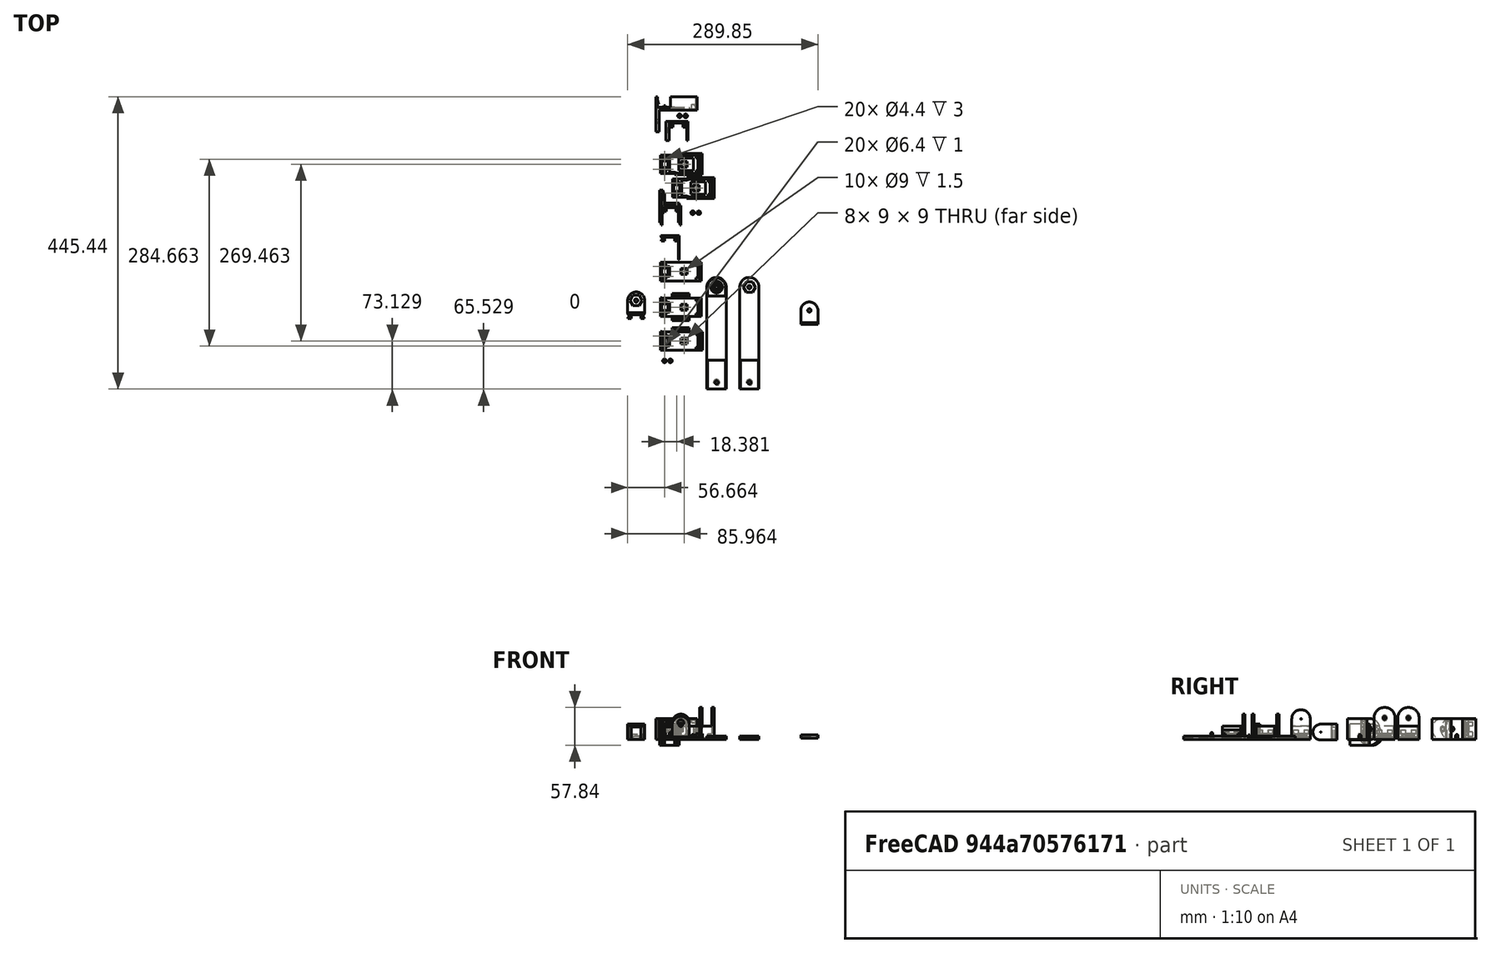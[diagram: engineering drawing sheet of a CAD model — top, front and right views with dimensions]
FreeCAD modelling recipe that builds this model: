
FCSTD DOCUMENT  (FreeCAD 0.18.4R)
Label: camera
License: All rights reserved
LicenseURL: http://en.wikipedia.org/wiki/All_rights_reserved
objects: Part::Extrusion×95, Part::Part2DObjectPython×85, Part::Feature×60, Part::MultiFuse×57, Part::FeaturePython×53, Part::Cut×43, App::DocumentObjectGroup×22, Part::MultiCommon×2, Part::Sphere×2, Part::Cone×1
note: 398 computed .brp shape members not serialized (recipe doc carries the construction recipe); baked Part::Feature solids carry a one-line shape summary decoded from their .brp

FEATURE [Part::MultiFuse] Fusion005002002014004003003002003
  Placement = pos=(31.9244,58.1866,-2) rot=(0,0,1;0rad)
FEATURE [Part::Feature] Fusion005002002014004003003001  label="Fusion005002002014004003004"
  shape: bbox 26 x 40.3 x 22 mm, 31 faces (baked)
FEATURE [Part::Part2DObjectPython] Rectangle  # Draft 2D object (typed FeaturePython)
  ChamferSize = 0
  Columns = 1
  FilletRadius = 0
  Height = 58
  Length = 28.2
  MakeFace = true
  Placement = pos=(-309.476,-65.7008,-5.13395) rot=(0.707107,0.707107,0;3.14159rad)
  Rows = 1
FEATURE [Part::Part2DObjectPython] Circle  # Draft 2D object (typed FeaturePython)
  FirstAngle = 0
  LastAngle = 0
  MakeFace = true
  Placement = pos=(-279.976,-51.6008,-5.13395) rot=(0.707107,0.707107,0;3.14159rad)
  Radius = 4.26
FEATURE [Part::Extrusion] Extrusion
  Base = -> Rectangle
  Dir = (0,0,2)
  DirMode = 0
  FaceMakerClass = Part::FaceMakerBullseye
  LengthFwd = 0
  LengthRev = 0
  Solid = true
  Symmetric = false
FEATURE [Part::Extrusion] Extrusion001
  Base = -> Circle
  Dir = (9.2e-15,2e-15,34.9207)
  DirMode = 0
  FaceMakerClass = Part::FaceMakerBullseye
  LengthFwd = 0
  LengthRev = 0
  Solid = true
  Symmetric = false
FEATURE [Part::Part2DObjectPython] Rectangle001  # Draft 2D object (typed FeaturePython)
  ChamferSize = 0
  Columns = 1
  FilletRadius = 0
  Height = 4.67245
  Length = 5.64116
  MakeFace = true
  Placement = pos=(-257.117,-65.7008,-3.13395) rot=(0,0,1;0rad)
  Rows = 1
FEATURE [Part::Extrusion] Extrusion002
  Base = -> Rectangle001
  Dir = (1.3e-15,3e-16,5)
  DirMode = 0
  FaceMakerClass = Part::FaceMakerBullseye
  LengthFwd = 0
  LengthRev = 0
  Solid = true
  Symmetric = false
FEATURE [Part::Cut] Cut001
  Base = -> Extrusion
  Tool = -> Extrusion001
FEATURE [Part::Part2DObjectPython] Rectangle002  # Draft 2D object (typed FeaturePython)
  ChamferSize = 0
  Columns = 1
  FilletRadius = 0
  Height = 4.67245
  Length = 5.64116
  MakeFace = true
  Placement = pos=(-257.117,-65.7008,-3.13395) rot=(0,0,1;0rad)
  Rows = 1
FEATURE [Part::Extrusion] Extrusion003
  Base = -> Rectangle002
  Dir = (1.3e-15,3e-16,5)
  DirMode = 0
  FaceMakerClass = Part::FaceMakerBullseye
  LengthFwd = 0
  LengthRev = 0
  Placement = pos=(0,23.5275,-1e-15) rot=(0,0,1;0rad)
  Solid = true
  Symmetric = false
FEATURE [Part::Feature] Fusion_solid  label="Fusion (Solid)"
  shape: bbox 58 x 28.2 x 3 mm, 16 faces (baked)
FEATURE [Part::Cut] Cut
  Base = -> Extrusion
  Tool = -> Extrusion001
FEATURE [Part::Part2DObjectPython] Rectangle003  # Draft 2D object (typed FeaturePython)
  ChamferSize = 0
  Columns = 1
  FilletRadius = 0
  Height = 9
  Length = 9
  MakeFace = true
  Placement = pos=(-284.476,-56.1008,-3.13395) rot=(0,0,1;0rad)
  Rows = 1
  Support = -> [Cut]
FEATURE [Part::Extrusion] Extrusion005
  Base = -> Rectangle003
  Dir = (-5e-16,-1e-16,-2)
  DirMode = 0
  FaceMakerClass = Part::FaceMakerBullseye
  LengthFwd = 0
  LengthRev = 0
  Solid = true
  Symmetric = false
FEATURE [Part::Cut] Cut002
  Base = -> Cut
  Tool = -> Extrusion005
FEATURE [Part::Feature] Fusion_solid001  label="Fusion (Solid)001"
  shape: bbox 58 x 28.2 x 3 mm, 12 faces (baked)
FEATURE [Part::MultiFuse] Fusion
  Shapes = -> [Fusion_solid001,Extrusion003,Extrusion002]
FEATURE [Part::Feature] Fusion005002002014004003003002004
  shape: bbox 58 x 28.2 x 8 mm, 18 faces (baked)
FEATURE [Part::Part2DObjectPython] Rectangle004  # Draft 2D object (typed FeaturePython)
  ChamferSize = 0
  Columns = 1
  FilletRadius = 0
  Height = 14
  Length = 28.2
  MakeFace = true
  Placement = pos=(-309.476,-65.7008,7.86605) rot=(0.57735,0.57735,-0.57735;4.18879rad)
  Rows = 1
  Support = -> [Fusion005002002014004003003002004]
FEATURE [Part::Extrusion] Extrusion006
  Base = -> Rectangle004
  Dir = (-2,0,0)
  DirMode = 0
  FaceMakerClass = Part::FaceMakerBullseye
  LengthFwd = 0
  LengthRev = 0
  Placement = pos=(-4.3,0,2.2e-15) rot=(0,0,1;0rad)
  Solid = true
  Symmetric = false
FEATURE [Part::Extrusion] Extrusion007
  Base = -> Rectangle004
  Dir = (-2,0,0)
  DirMode = 0
  FaceMakerClass = Part::FaceMakerBullseye
  LengthFwd = 0
  LengthRev = 0
  Placement = pos=(60,-1.4e-14,-1.3e-14) rot=(0,0,1;0rad)
  Solid = true
  Symmetric = false
FEATURE [Part::Feature] Face
  shape: bbox 2e-07 x 28.2 x 3 mm, 1 faces, 0 solids (baked)
FEATURE [Part::Extrusion] Extrusion008
  Base = -> Face
  Dir = (-4.3,0,0)
  DirMode = 0
  FaceMakerClass = Part::FaceMakerBullseye
  LengthFwd = 0
  LengthRev = 0
  Solid = true
  Symmetric = false
FEATURE [Part::Part2DObjectPython] Rectangle005  # Draft 2D object (typed FeaturePython)
  ChamferSize = 0
  Columns = 1
  FilletRadius = 0
  Height = 36.0595
  Length = 50.5086
  MakeFace = true
  Placement = pos=(-257.117,-34.3271,-15.1061) rot=(0.57735,-0.57735,-0.57735;2.0944rad)
  Rows = 1
  Support = -> [Fusion005002002014004003003002004]
FEATURE [Part::FeaturePython] Slice  # WARN: FeaturePython — macro-defined, semantics opaque (R4)
  Base = -> Fusion005002002014004003003002004
  Mode = 1
  Tolerance = 0
  Tools = -> [Rectangle005]
FEATURE [App::DocumentObjectGroup] GrExplode_Slice  label="Exploded Slice"
FEATURE [Part::FeaturePython] Slice_child0  label="Slice.0"  # WARN: FeaturePython — macro-defined, semantics opaque (R4)
  Base = -> Slice
  FilterType = 1
  Invert = false
  OverrideMaxVal = 0
  WindowFrom = 80
  WindowTo = 100
  items = 0
FEATURE [Part::FeaturePython] Slice_child1  label="Slice.1"  # WARN: FeaturePython — macro-defined, semantics opaque (R4)
  Base = -> Slice
  FilterType = 1
  Invert = false
  OverrideMaxVal = 0
  WindowFrom = 80
  WindowTo = 100
  items = 1
FEATURE [Part::MultiFuse] Fusion005002002014004003003002005
  Placement = pos=(-4.5,0,4e-15) rot=(0,0,1;0rad)
  Shapes = -> [Slice_child1,Extrusion007]
FEATURE [Part::Part2DObjectPython] Rectangle006  # Draft 2D object (typed FeaturePython)
  ChamferSize = 0
  Columns = 1
  FilletRadius = 0
  Height = 4
  Length = 9
  MakeFace = true
  Placement = pos=(-313.776,-56.1008,-2.13395) rot=(0.57735,0.57735,0.57735;2.0944rad)
  Rows = 1
FEATURE [Part::Extrusion] Extrusion009
  Base = -> Rectangle006
  Dir = (-21.3643,0,0)
  DirMode = 0
  FaceMakerClass = Part::FaceMakerBullseye
  LengthFwd = 0
  LengthRev = 0
  Solid = true
  Symmetric = false
FEATURE [Part::Cut] Cut003
  Base = -> Extrusion006
  Tool = -> Extrusion009
FEATURE [Part::Part2DObjectPython] Rectangle007  # Draft 2D object (typed FeaturePython)
  ChamferSize = 0
  Columns = 1
  FilletRadius = 0
  Height = 1.5
  Length = 2.82058
  MakeFace = true
  Placement = pos=(-258.797,-42.1733,0.366052) rot=(1,0,0;1.5708rad)
  Rows = 1
  Support = -> [Fusion005002002014004003003002005]
FEATURE [Part::Extrusion] Extrusion010
  Base = -> Rectangle007
  Dir = (1.8e-15,-18.8551,4.2e-15)
  DirMode = 0
  FaceMakerClass = Part::FaceMakerBullseye
  LengthFwd = 0
  LengthRev = 0
  Solid = true
  Symmetric = false
FEATURE [Part::Part2DObjectPython] Wire001  # Draft 2D object (typed FeaturePython)
  ChamferSize = 0
  Closed = true
  End = (-313.776,-37.5008,1.86605)
  FilletRadius = 0
  Length = 3.58114
  MakeFace = true
  Placement = pos=(-313.776,-37.5008,3.36605) rot=(0.57735,0.57735,0.57735;2.0944rad)
  Points = (3) [(0,0,0),(0,-1.5,0.5),(0,-1.5,0)]
  Start = (-313.776,-37.5008,3.36605)
  Subdivisions = 0
FEATURE [Part::Extrusion] Extrusion011
  Base = -> Wire001
  Dir = (0,-28.2,0)
  DirMode = 0
  FaceMakerClass = Part::FaceMakerBullseye
  LengthFwd = 0
  LengthRev = 0
  Solid = true
  Symmetric = false
FEATURE [Part::Part2DObjectPython] Rectangle008  # Draft 2D object (typed FeaturePython)
  ChamferSize = 0
  Columns = 1
  FilletRadius = 0
  Height = 15.7414
  Length = 21.4214
  MakeFace = true
  Placement = pos=(-300.219,-56.1008,-2.25209) rot=(0,0.707107,0.707107;3.14159rad)
  Rows = 1
  Support = -> [Cut003]
FEATURE [Part::FeaturePython] Slice001  # WARN: FeaturePython — macro-defined, semantics opaque (R4)
  Base = -> Extrusion011
  Mode = 1
  Tolerance = 0
  Tools = -> [Rectangle008]
FEATURE [Part::FeaturePython] Slice001_child0  label="Slice001.0"  # WARN: FeaturePython — macro-defined, semantics opaque (R4)
  Base = -> Slice001
  FilterType = 1
  Invert = false
  OverrideMaxVal = 0
  WindowFrom = 80
  WindowTo = 100
  items = 0
FEATURE [Part::FeaturePython] Slice001_child1  label="Slice001.1"  # WARN: FeaturePython — macro-defined, semantics opaque (R4)
  Base = -> Slice001
  FilterType = 1
  Invert = false
  OverrideMaxVal = 0
  WindowFrom = 80
  WindowTo = 100
  items = 1
FEATURE [Part::Part2DObjectPython] Rectangle009  # Draft 2D object (typed FeaturePython)
  ChamferSize = 0
  Columns = 1
  FilletRadius = 0
  Height = 15.162
  Length = 26.3983
  MakeFace = true
  Placement = pos=(-330.254,-47.1008,-3.77324) rot=(1,0,0;1.5708rad)
  Rows = 1
  Support = -> [Cut003]
FEATURE [Part::FeaturePython] Slice002  # WARN: FeaturePython — macro-defined, semantics opaque (R4)
  Base = -> Slice001_child0
  Mode = 1
  Tolerance = 0
  Tools = -> [Rectangle009]
FEATURE [App::DocumentObjectGroup] GrExplode_Slice002  label="Exploded Slice002"
FEATURE [Part::FeaturePython] Slice002_child0  label="Slice002.0"  # WARN: FeaturePython — macro-defined, semantics opaque (R4)
  Base = -> Slice002
  FilterType = 1
  Invert = false
  OverrideMaxVal = 0
  WindowFrom = 80
  WindowTo = 100
  items = 0
FEATURE [Part::MultiFuse] Fusion005002002014004003003002006
  Shapes = -> [Slice_child0,Cut003]
FEATURE [Part::MultiFuse] Fusion005002002014004003003002007
  Shapes = -> [Fusion005002002014004003003002006,Extrusion008,Slice002_child0,Slice001_child1]
FEATURE [Part::MultiFuse] Fusion005002002014004003003002008
  Shapes = -> [Extrusion010,Fusion005002002014004003003002005,Fusion005002002014004003003002007]
FEATURE [App::DocumentObjectGroup] GrExplode_Slice001  label="Exploded Slice001"
  Group = -> [Slice001_child0,Fusion005002002014004003003002008]
FEATURE [Part::Part2DObjectPython] Rectangle010  # Draft 2D object (typed FeaturePython)
  ChamferSize = 0
  Columns = 1
  FilletRadius = 0
  Height = 53.4258
  Length = 85.86
  MakeFace = true
  Placement = pos=(-132.272,-50.1607,-0.133948) rot=(0,0,1;0rad)
  Rows = 1
  Support = -> [Fusion005002002014004003003001]
FEATURE [Part::FeaturePython] Slice003  # WARN: FeaturePython — macro-defined, semantics opaque (R4)
  Base = -> Fusion005002002014004003003001
  Mode = 1
  Tolerance = 0
  Tools = -> [Rectangle010]
FEATURE [Part::FeaturePython] Slice003_child0  label="Slice003.0"  # WARN: FeaturePython — macro-defined, semantics opaque (R4)
  Base = -> Slice003
  FilterType = 1
  Invert = false
  OverrideMaxVal = 0
  WindowFrom = 80
  WindowTo = 100
  items = 0
FEATURE [App::DocumentObjectGroup] GrExplode_Slice003  label="Exploded Slice003"
  Group = -> [Slice003_child0]
FEATURE [Part::Part2DObjectPython] Rectangle011  # Draft 2D object (typed FeaturePython)
  ChamferSize = 0
  Columns = 1
  FilletRadius = 0
  Height = 50.1194
  Length = 61.469
  MakeFace = true
  Placement = pos=(-118.558,-26.4473,-37.364) rot=(1,0,0;1.5708rad)
  Rows = 1
  Support = -> [Slice003_child0]
FEATURE [Part::FeaturePython] Slice004  # WARN: FeaturePython — macro-defined, semantics opaque (R4)
  Base = -> Slice003_child0
  Mode = 1
  Tolerance = 0
  Tools = -> [Rectangle011]
FEATURE [Part::FeaturePython] Slice004_child1  label="Slice004.1"  # WARN: FeaturePython — macro-defined, semantics opaque (R4)
  Base = -> Slice004
  FilterType = 1
  Invert = false
  OverrideMaxVal = 0
  WindowFrom = 80
  WindowTo = 100
  items = 1
FEATURE [Part::Feature] Face001
  shape: bbox 9.594e-07 x 1.6 x 5 mm, 1 faces, 0 solids (baked)
FEATURE [Part::Extrusion] Extrusion012
  Base = -> Face001
  Dir = (25,1.785e-13,-4e-15)
  DirMode = 0
  FaceMakerClass = Part::FaceMakerBullseye
  LengthFwd = 0
  LengthRev = 0
  Solid = true
  Symmetric = false
FEATURE [Part::Cut] Cut004
  Base = -> Slice004_child1
  Tool = -> Extrusion012
FEATURE [Part::Part2DObjectPython] Rectangle012  # Draft 2D object (typed FeaturePython)
  ChamferSize = 0
  Columns = 1
  FilletRadius = 0
  Height = 5
  Length = 26
  MakeFace = true
  Placement = pos=(-102.092,-24.8473,-5.13395) rot=(1,0,0;1.5708rad)
  Rows = 1
  Support = -> [Cut004]
FEATURE [Part::Extrusion] Extrusion013
  Base = -> Rectangle012
  Dir = (8.5e-15,-1.60055,-1.1e-15)
  DirMode = 0
  FaceMakerClass = Part::FaceMakerBullseye
  LengthFwd = 0
  LengthRev = 0
  Solid = true
  Symmetric = false
FEATURE [Part::MultiFuse] Fusion005002002014004003003002009
  Shapes = -> [Cut004,Extrusion013]
FEATURE [App::DocumentObjectGroup] GrExplode_Slice004  label="Exploded Slice004"
  Group = -> [Fusion005002002014004003003002009]
FEATURE [Part::Feature] Fusion005002002014004003003002009001  label="Fusion005002002014004003003002010"
  Placement = pos=(-195.784,-37.6348,20.3139) rot=(1,0,0;1.5708rad)
  shape: bbox 26 x 5 x 34.5 mm, 11 faces (baked)
FEATURE [Part::Feature] Fusion005002002014004003003002008001  label="Fusion005002002014004003003002011"
  shape: bbox 61.8 x 28.2 x 14 mm, 35 faces (baked)
FEATURE [Part::MultiFuse] Fusion005002002014004003003002009002
  Shapes = -> [Fusion005002002014004003003002008001,Fusion005002002014004003003002009001]
FEATURE [Part::Feature] Fusion005002002014004003003002009002001  label="Fusion005002002014004003003002009003"
  shape: bbox 61.8 x 33.2 x 34.5 mm, 46 faces (baked)
FEATURE [Part::Part2DObjectPython] Wire002  # Draft 2D object (typed FeaturePython)
  ChamferSize = 0
  Closed = true
  End = (-313.776,-65.7008,1.86605)
  FilletRadius = 0
  Length = 6.19258
  MakeFace = true
  Placement = pos=(-312.776,-65.7008,1.86605) rot=(1,0,0;1.5708rad)
  Points = (3) [(0,0,0),(-1,2.5,0),(-1,4.44089e-16,0)]
  Start = (-312.776,-65.7008,1.86605)
  Subdivisions = 0
  Support = -> [Fusion005002002014004003003002009002001]
FEATURE [Part::Part2DObjectPython] Wire003  # Draft 2D object (typed FeaturePython)
  ChamferSize = 0
  Closed = true
  End = (-313.776,-47.1008,1.86605)
  FilletRadius = 0
  Length = 6.19258
  MakeFace = true
  Placement = pos=(-312.776,-47.1008,1.86605) rot=(1,0,0;1.5708rad)
  Points = (3) [(0,0,0),(-1,2.5,0),(-1,4.44089e-16,0)]
  Start = (-312.776,-47.1008,1.86605)
  Subdivisions = 0
  Support = -> [Fusion005002002014004003003002009002001]
FEATURE [Part::Extrusion] Extrusion014
  Base = -> Wire002
  Dir = (2.9e-15,9.6,-2.1e-15)
  DirMode = 0
  FaceMakerClass = Part::FaceMakerBullseye
  LengthFwd = 0
  LengthRev = 0
  Solid = true
  Symmetric = false
FEATURE [Part::Extrusion] Extrusion015
  Base = -> Wire003
  Dir = (0,9.6,-2.1e-15)
  DirMode = 0
  FaceMakerClass = Part::FaceMakerBullseye
  LengthFwd = 0
  LengthRev = 0
  Solid = true
  Symmetric = false
FEATURE [Part::MultiFuse] Fusion005002002014004003003002009002002
  Shapes = -> [Extrusion015,Extrusion014,Fusion005002002014004003003002009002001]
FEATURE [Part::Part2DObjectPython] Circle001  # Draft 2D object (typed FeaturePython)
  FirstAngle = 0
  LastAngle = 0
  MakeFace = true
  Placement = pos=(-279.976,-51.6008,-6.13395) rot=(1,0,0;3.14159rad)
  Radius = 4.3
  Support = -> [Fusion005002002014004003003002009002002]
FEATURE [Part::Extrusion] Extrusion016
  Base = -> Circle001
  Dir = (-4.6e-15,1.7e-15,28.4469)
  DirMode = 0
  FaceMakerClass = Part::FaceMakerBullseye
  LengthFwd = 0
  LengthRev = 0
  Solid = true
  Symmetric = false
FEATURE [Part::Cut] Cut005
  Base = -> Fusion005002002014004003003002009002002
  Tool = -> Extrusion016
FEATURE [Part::Part2DObjectPython] Rectangle013  # Draft 2D object (typed FeaturePython)
  ChamferSize = 0
  Columns = 1
  FilletRadius = 0
  Height = 39.7771
  Length = 42.4358
  MakeFace = true
  Placement = pos=(-306.094,-54.3894,-0.133948) rot=(0,0,1;0rad)
  Rows = 1
  Support = -> [Cut005]
FEATURE [Part::FeaturePython] Slice005  # WARN: FeaturePython — macro-defined, semantics opaque (R4)
  Base = -> Cut005
  Mode = 1
  Tolerance = 0
  Tools = -> [Rectangle013]
FEATURE [Part::FeaturePython] Slice005_child0  label="Slice005.0"  # WARN: FeaturePython — macro-defined, semantics opaque (R4)
  Base = -> Slice005
  FilterType = 1
  Invert = false
  OverrideMaxVal = 0
  WindowFrom = 80
  WindowTo = 100
  items = 0
FEATURE [Part::FeaturePython] Slice005_child1  label="Slice005.1"  # WARN: FeaturePython — macro-defined, semantics opaque (R4)
  Base = -> Slice005
  FilterType = 1
  Invert = false
  OverrideMaxVal = 0
  Placement = pos=(0,-7.1e-15,5) rot=(0,0,1;0rad)
  WindowFrom = 80
  WindowTo = 100
  items = 1
FEATURE [Part::Feature] Face002
  shape: bbox 26 x 2 x 1.159e-06 mm, 1 faces, 0 solids (baked)
FEATURE [Part::Extrusion] Extrusion017
  Base = -> Face002
  Dir = (1.2e-15,3e-16,5)
  DirMode = 0
  FaceMakerClass = Part::FaceMakerBullseye
  LengthFwd = 0
  LengthRev = 0
  Solid = true
  Symmetric = false
FEATURE [Part::MultiFuse] Fusion005002002014004003003002009002003
  Shapes = -> [Extrusion017,Slice005_child1,Slice005_child0]
FEATURE [App::DocumentObjectGroup] GrExplode_Slice005  label="Exploded Slice005"
  Group = -> [Fusion005002002014004003003002009002003]
FEATURE [Part::MultiFuse] Fusion005002002014004003003002009002004
  Placement = pos=(51.6645,21.162,-2.49e-14) rot=(0,0,1;0rad)
FEATURE [Part::Part2DObjectPython] Rectangle014  # Draft 2D object (typed FeaturePython)
  ChamferSize = 0
  Columns = 1
  FilletRadius = 0
  Height = 19.6703
  Length = 47.7725
  MakeFace = true
  Placement = pos=(-234.567,-20.1251,8.20122) rot=(-1,0,0;1.5708rad)
  Rows = 1
  Support = -> [Fusion005002002014004003003002009002003]
FEATURE [Part::FeaturePython] Slice006  # WARN: FeaturePython — macro-defined, semantics opaque (R4)
  Base = -> Fusion005002002014004003003002009002004
  Mode = 1
  Tolerance = 0
  Tools = -> [Rectangle014]
FEATURE [App::DocumentObjectGroup] GrExplode_Slice006  label="Exploded Slice006"
FEATURE [Part::FeaturePython] Slice006_child1  label="Slice006.1"  # WARN: FeaturePython — macro-defined, semantics opaque (R4)
  Base = -> Slice006
  FilterType = 1
  Invert = false
  OverrideMaxVal = 0
  WindowFrom = 80
  WindowTo = 100
  items = 1
FEATURE [Part::Feature] Face003
  Placement = pos=(-15.6247,58.8384,-1.39e-14) rot=(0,0,1;0rad)
  shape: bbox 18 x 18 x 1.133e-06 mm, 1 faces, 0 solids (baked)
FEATURE [Part::Extrusion] Extrusion018
  Base = -> Face003
  Dir = (-7e-16,8e-16,-2)
  DirMode = 0
  FaceMakerClass = Part::FaceMakerBullseye
  LengthFwd = 0
  LengthRev = 0
  Solid = true
  Symmetric = false
FEATURE [Part::Feature] Face004
  shape: bbox 29.42 x 28.42 x 1.743e-06 mm, 1 faces, 0 solids (baked)
FEATURE [Part::Extrusion] Extrusion019
  Base = -> Face004
  Dir = (-7e-16,8e-16,-2)
  DirMode = 0
  FaceMakerClass = Part::FaceMakerBullseye
  LengthFwd = 0
  LengthRev = 0
  Solid = true
  Symmetric = false
FEATURE [Part::Cut] Cut006
  Base = -> Slice006_child1
  Tool = -> Extrusion019
FEATURE [Part::Cut] Cut007
  Base = -> Cut006
  Placement = pos=(0,-25.259,14.9911) rot=(1,0,0;1.5708rad)
  Tool = -> Extrusion018
FEATURE [Part::Part2DObjectPython] Rectangle015  # Draft 2D object (typed FeaturePython)
  ChamferSize = 0
  Columns = 1
  FilletRadius = 0
  Height = 22.6431
  Length = 32.3653
  MakeFace = true
  Placement = pos=(-301.059,-45.8224,4.86605) rot=(0,0,1;0rad)
  Rows = 1
  Support = -> [Fusion005002002014004003003002009002003]
FEATURE [Part::FeaturePython] Slice007  # WARN: FeaturePython — macro-defined, semantics opaque (R4)
  Base = -> Fusion005002002014004003003002009002003
  Mode = 1
  Tolerance = 0
  Tools = -> [Rectangle015]
FEATURE [Part::FeaturePython] Slice007_child0  label="Slice007.0"  # WARN: FeaturePython — macro-defined, semantics opaque (R4)
  Base = -> Slice007
  FilterType = 1
  Invert = false
  OverrideMaxVal = 0
  WindowFrom = 80
  WindowTo = 100
  items = 0
FEATURE [Part::Part2DObjectPython] Circle002  # Draft 2D object (typed FeaturePython)
  FirstAngle = 0
  LastAngle = 0
  MakeFace = true
  Placement = pos=(-210.723,-23.6251,8.57368) rot=(1,0,0;1.5708rad)
  Radius = 13.7076
  Support = -> [Cut007]
FEATURE [Part::Part2DObjectPython] Rectangle016  # Draft 2D object (typed FeaturePython)
  ChamferSize = 0
  Columns = 1
  FilletRadius = 0
  Height = 13.7076
  Length = 27.4152
  MakeFace = true
  Placement = pos=(-224.431,-23.6251,-5.13395) rot=(1,0,0;1.5708rad)
  Rows = 1
FEATURE [Part::Extrusion] Extrusion020
  Base = -> Rectangle016
  Dir = (5e-16,17.7755,-1.38e-14)
  DirMode = 0
  FaceMakerClass = Part::FaceMakerBullseye
  LengthFwd = 0
  LengthRev = 0
  Solid = true
  Symmetric = false
FEATURE [Part::Extrusion] Extrusion021
  Base = -> Circle002
  Dir = (5e-16,17.7755,-1.38e-14)
  DirMode = 0
  FaceMakerClass = Part::FaceMakerBullseye
  LengthFwd = 0
  LengthRev = 0
  Solid = true
  Symmetric = false
FEATURE [Part::MultiFuse] Fusion005002002014004003003002009002005
  Shapes = -> [Extrusion020,Extrusion021]
FEATURE [Part::MultiCommon] Common
  Placement = pos=(-74.153,-10.8758,10) rot=(0,0,1;0rad)
  Shapes = -> [Fusion005002002014004003003002009002005,Cut007]
FEATURE [Part::Part2DObjectPython] Rectangle017  # Draft 2D object (typed FeaturePython)
  ChamferSize = 0
  Columns = 1
  FilletRadius = 0
  Height = 13.7076
  Length = 26
  MakeFace = true
  Placement = pos=(-297.876,-34.5008,4.86605) rot=(1,0,0;1.5708rad)
  Rows = 1
FEATURE [Part::Part2DObjectPython] Circle003  # Draft 2D object (typed FeaturePython)
  FirstAngle = 0
  LastAngle = 0
  MakeFace = true
  Placement = pos=(-284.876,-34.5008,18.5737) rot=(1,0,0;1.5708rad)
  Radius = 13
FEATURE [Part::Extrusion] Extrusion022
  Base = -> Circle003
  Dir = (9e-16,15.2336,-1.18e-14)
  DirMode = 0
  FaceMakerClass = Part::FaceMakerBullseye
  LengthFwd = 0
  LengthRev = 0
  Solid = true
  Symmetric = false
FEATURE [Part::Extrusion] Extrusion023
  Base = -> Rectangle017
  Dir = (9e-16,15.2336,-1.18e-14)
  DirMode = 0
  FaceMakerClass = Part::FaceMakerBullseye
  LengthFwd = 0
  LengthRev = 0
  Solid = true
  Symmetric = false
FEATURE [Part::MultiFuse] Fusion005002002014004003003002009002006
  Shapes = -> [Extrusion022,Extrusion023]
FEATURE [Part::MultiCommon] Common001
  Shapes = -> [Common,Fusion005002002014004003003002009002006]
FEATURE [Part::Feature] Face005
  shape: bbox 13 x 3.5 x 1.743e-06 mm, 1 faces, 0 solids (baked)
FEATURE [Part::Extrusion] Extrusion024
  Base = -> Face005
  Dir = (3e-16,-8.5e-15,-11)
  DirMode = 0
  FaceMakerClass = Part::FaceMakerBullseye
  LengthFwd = 0
  LengthRev = 0
  Solid = true
  Symmetric = false
FEATURE [Part::Feature] Face006
  shape: bbox 13 x 3.5 x 1.743e-06 mm, 1 faces, 0 solids (baked)
FEATURE [Part::Extrusion] Extrusion025
  Base = -> Face006
  Dir = (3e-16,-8.5e-15,-11)
  DirMode = 0
  FaceMakerClass = Part::FaceMakerBullseye
  LengthFwd = 0
  LengthRev = 0
  Solid = true
  Symmetric = false
FEATURE [Part::MultiFuse] Fusion005002002014004003003002009002007
  Shapes = -> [Extrusion024,Extrusion025,Common001]
FEATURE [Part::MultiFuse] Fusion005002002014004003003002009002008
  Shapes = -> [Fusion005002002014004003003002009002007,Slice007_child0]
FEATURE [Part::Feature] Face007
  shape: bbox 9 x 9 x 2e-07 mm, 1 faces, 0 solids (baked)
FEATURE [Part::Extrusion] Extrusion026
  Base = -> Face007
  Dir = (0,0,-0.5)
  DirMode = 0
  FaceMakerClass = Part::FaceMakerBullseye
  LengthFwd = 0
  LengthRev = 0
  Solid = true
  Symmetric = false
FEATURE [Part::Cut] Cut008
  Base = -> Fusion005002002014004003003002009002008
  Tool = -> Extrusion026
FEATURE [Part::Part2DObjectPython] Circle004  # Draft 2D object (typed FeaturePython)
  FirstAngle = 0
  LastAngle = 0
  MakeFace = true
  Placement = pos=(-309.276,-59.2008,-3.13395) rot=(0,0,1;0rad)
  Radius = 2
FEATURE [Part::Part2DObjectPython] Circle005  # Draft 2D object (typed FeaturePython)
  FirstAngle = 0
  LastAngle = 0
  MakeFace = true
  Placement = pos=(-309.276,-44.0008,-3.13395) rot=(0,0,1;0rad)
  Radius = 2
  Support = -> [Circle004]
FEATURE [Part::Extrusion] Extrusion027
  Base = -> Circle004
  Dir = (-4.6e-15,-1.2e-15,-20.0047)
  DirMode = 0
  FaceMakerClass = Part::FaceMakerBullseye
  LengthFwd = 0
  LengthRev = 0
  Solid = true
  Symmetric = false
FEATURE [Part::Extrusion] Extrusion028
  Base = -> Circle005
  Dir = (-1e-14,-2.6e-15,-43.2692)
  DirMode = 0
  FaceMakerClass = Part::FaceMakerBullseye
  LengthFwd = 0
  LengthRev = 0
  Solid = true
  Symmetric = false
FEATURE [Part::Cut] Cut009
  Base = -> Cut008
  Tool = -> Extrusion027
FEATURE [Part::Cut] Cut010
  Base = -> Cut009
  Tool = -> Extrusion028
FEATURE [App::DocumentObjectGroup] GrExplode_Slice007  label="Exploded Slice007"
  Group = -> [Cut010]
FEATURE [Part::Feature] Cut010001  label="Cut011"
  shape: bbox 61.8 x 34.7 x 37.71 mm, 48 faces (baked)
FEATURE [Part::Feature] Face008
  shape: bbox 61.8 x 34.7 x 1.743e-06 mm, 1 faces, 0 solids (baked)
FEATURE [Part::Extrusion] Extrusion029
  Base = -> Face008
  Dir = (0,-1.1e-15,-1)
  DirMode = 0
  FaceMakerClass = Part::FaceMakerBullseye
  LengthFwd = 0
  LengthRev = 0
  Solid = true
  Symmetric = false
FEATURE [Part::MultiFuse] Fusion005002002014004003003002009002009
  Shapes = -> [Cut010001,Extrusion029]
FEATURE [Part::Part2DObjectPython] Rectangle018  # Draft 2D object (typed FeaturePython)
  ChamferSize = 0
  Columns = 1
  FilletRadius = 0
  Height = 15.2
  Length = 3
  MakeFace = true
  Placement = pos=(-304.776,-59.2008,-3.13395) rot=(0,0,1;0rad)
  Rows = 1
FEATURE [Part::Extrusion] Extrusion030
  Base = -> Rectangle018
  Dir = (8e-16,2e-16,3.5)
  DirMode = 0
  FaceMakerClass = Part::FaceMakerBullseye
  LengthFwd = 0
  LengthRev = 0
  Solid = true
  Symmetric = false
FEATURE [Part::MultiFuse] Fusion005002002014004003003002009002010
  Shapes = -> [Fusion005002002014004003003002009002009,Extrusion030]
FEATURE [Part::Feature] Fusion005002002014004003003002009002010001  label="Fusion005002002014004003003002009002011"
  shape: bbox 61.8 x 34.7 x 38.71 mm, 53 faces (baked)
FEATURE [Part::Part2DObjectPython] Circle006  # Draft 2D object (typed FeaturePython)
  FirstAngle = 0
  LastAngle = 0
  MakeFace = true
  Placement = pos=(-309.276,-59.2008,-3.13395) rot=(0,0,1;0rad)
  Radius = 3
  Support = -> [Fusion005002002014004003003002009002010001]
FEATURE [Part::Part2DObjectPython] Circle007  # Draft 2D object (typed FeaturePython)
  FirstAngle = 0
  LastAngle = 0
  MakeFace = true
  Placement = pos=(-309.276,-44.0008,-3.13395) rot=(0,0,1;0rad)
  Radius = 3
  Support = -> [Circle006]
FEATURE [Part::Extrusion] Extrusion031
  Base = -> Circle006
  Dir = (-2e-16,-1e-16,-1)
  DirMode = 0
  FaceMakerClass = Part::FaceMakerBullseye
  LengthFwd = 0
  LengthRev = 0
  Solid = true
  Symmetric = false
FEATURE [Part::Extrusion] Extrusion032
  Base = -> Circle007
  Dir = (-2e-16,-1e-16,-1)
  DirMode = 0
  FaceMakerClass = Part::FaceMakerBullseye
  LengthFwd = 0
  LengthRev = 0
  Solid = true
  Symmetric = false
FEATURE [Part::Cut] Cut010002
  Base = -> Fusion005002002014004003003002009002010001
  Tool = -> Extrusion031
FEATURE [Part::Cut] Cut010003
  Base = -> Cut010002
  Tool = -> Extrusion032
FEATURE [Part::Part2DObjectPython] Circle008  # Draft 2D object (typed FeaturePython)
  FirstAngle = 0
  LastAngle = 0
  MakeFace = true
  Placement = pos=(-309.772,-81.7351,-7.13395) rot=(1,0,0;3.14159rad)
  Radius = 2.8
  Support = -> [Cut010003]
FEATURE [Part::Extrusion] Extrusion033
  Base = -> Circle008
  Dir = (1e-16,3.4e-15,3)
  DirMode = 0
  FaceMakerClass = Part::FaceMakerBullseye
  LengthFwd = 0
  LengthRev = 0
  Solid = true
  Symmetric = false
FEATURE [Part::Part2DObjectPython] Circle009  # Draft 2D object (typed FeaturePython)
  FirstAngle = 0
  LastAngle = 0
  MakeFace = true
  Placement = pos=(-309.772,-81.7351,-4.13395) rot=(0,0,1;0rad)
  Radius = 1.8
  Support = -> [Extrusion033]
FEATURE [Part::Extrusion] Extrusion034
  Base = -> Circle009
  Dir = (0,0,6)
  DirMode = 0
  FaceMakerClass = Part::FaceMakerBullseye
  LengthFwd = 0
  LengthRev = 0
  Solid = true
  Symmetric = false
FEATURE [Part::MultiFuse] Fusion005002002014004003003002009002010002
  Placement = pos=(8.93208,0,0) rot=(0,0,1;0rad)
  Shapes = -> [Extrusion033,Extrusion034]
FEATURE [Part::MultiFuse] Fusion005002002014004003003002009002010003
  Shapes = -> [Extrusion033,Extrusion034]
FEATURE [Part::Part2DObjectPython] Circle010  # Draft 2D object (typed FeaturePython)
  FirstAngle = 0
  LastAngle = 0
  MakeFace = true
  Placement = pos=(-279.976,-51.6008,-5.63395) rot=(1,0,0;3.14159rad)
  Radius = 4.5
  Support = -> [Cut010003]
FEATURE [Part::Extrusion] Extrusion035
  Base = -> Circle010
  Dir = (-1e-15,-3.83e-14,-34.2405)
  DirMode = 0
  FaceMakerClass = Part::FaceMakerBullseye
  LengthFwd = 0
  LengthRev = 0
  Solid = true
  Symmetric = false
FEATURE [Part::Cut] Cut010004
  Base = -> Cut010003
  Tool = -> Extrusion035
FEATURE [Part::Part2DObjectPython] Wire  # Draft 2D object (typed FeaturePython)
  ChamferSize = 0
  Closed = true
  End = (-313.776,-65.7008,1.86605)
  FilletRadius = 0
  Length = 6.19258
  MakeFace = true
  Placement = pos=(-313.776,-65.7008,4.36605) rot=(0.57735,0.57735,0.57735;2.0944rad)
  Points = (3) [(0,0,0),(0,-2.5,1),(0,-2.5,0)]
  Start = (-313.776,-65.7008,4.36605)
  Subdivisions = 0
FEATURE [Part::Extrusion] Extrusion036
  Base = -> Wire
  Dir = (0,3,0)
  DirMode = 0
  FaceMakerClass = Part::FaceMakerBullseye
  LengthFwd = 0
  LengthRev = 0
  Solid = true
  Symmetric = false
FEATURE [Part::Extrusion] Extrusion037
  Base = -> Wire
  Dir = (0,3,0)
  DirMode = 0
  FaceMakerClass = Part::FaceMakerBullseye
  LengthFwd = 0
  LengthRev = 0
  Placement = pos=(0,25.2,9.8e-15) rot=(0,0,1;0rad)
  Solid = true
  Symmetric = false
FEATURE [Part::Cut] Cut010005
  Base = -> Cut010004
  Tool = -> Extrusion037
FEATURE [Part::Cut] Cut010006
  Base = -> Cut010005
  Tool = -> Extrusion036
FEATURE [Part::Feature] Face009
  Placement = pos=(31.9244,58.1866,-2) rot=(0,0,1;0rad)
  shape: bbox 27.5 x 37.68 x 1.867e-06 mm, 1 faces, 0 solids (baked)
FEATURE [Part::Extrusion] Extrusion038
  Base = -> Face009
  Dir = (0,4e-16,2)
  DirMode = 0
  FaceMakerClass = Part::FaceMakerBullseye
  LengthFwd = 0
  LengthRev = 0
  Solid = true
  Symmetric = false
FEATURE [Part::MultiFuse] Fusion005002002014004003003002009002010004
  Shapes = -> [Extrusion038,Fusion005002002014004003003002003]
FEATURE [Part::Feature] Fusion005002002014004003003002009002010004001  label="Fusion005002002014004003003002009002010005"
  Placement = pos=(50.0081,0,-2.22e-14) rot=(0,0,1;0rad)
  shape: bbox 29.42 x 170 x 5.5 mm, 22 faces (baked)
FEATURE [Part::Part2DObjectPython] Circle011  # Draft 2D object (typed FeaturePython)
  FirstAngle = 0
  LastAngle = 0
  MakeFace = true
  Placement = pos=(-309.276,-59.2008,-4.13395) rot=(0,0,1;0rad)
  Radius = 2.2
  Support = -> [Cut010006]
FEATURE [Part::Part2DObjectPython] Circle012  # Draft 2D object (typed FeaturePython)
  FirstAngle = 0
  LastAngle = 0
  MakeFace = true
  Placement = pos=(-309.276,-44.0008,-4.13395) rot=(0,0,1;0rad)
  Radius = 2.2
  Support = -> [Circle011]
FEATURE [Part::Extrusion] Extrusion039
  Base = -> Circle011
  Dir = (0,0,-61.6597)
  DirMode = 0
  FaceMakerClass = Part::FaceMakerBullseye
  LengthFwd = 0
  LengthRev = 0
  Solid = true
  Symmetric = false
FEATURE [Part::Extrusion] Extrusion040
  Base = -> Circle012
  Dir = (0,0,-67.9147)
  DirMode = 0
  FaceMakerClass = Part::FaceMakerBullseye
  LengthFwd = 0
  LengthRev = 0
  Solid = true
  Symmetric = false
FEATURE [Part::Cut] Cut010007
  Base = -> Cut010006
  Tool = -> Extrusion039
FEATURE [Part::Cut] Cut010008
  Base = -> Cut010007
  Tool = -> Extrusion040
FEATURE [Part::Part2DObjectPython] Circle013  # Draft 2D object (typed FeaturePython)
  FirstAngle = 0
  LastAngle = 0
  MakeFace = true
  Placement = pos=(-309.276,-59.2008,-4.13395) rot=(0,0,1;0rad)
  Radius = 3.2
  Support = -> [Cut010008]
FEATURE [Part::Part2DObjectPython] Circle014  # Draft 2D object (typed FeaturePython)
  FirstAngle = 0
  LastAngle = 0
  MakeFace = true
  Placement = pos=(-309.276,-44.0008,-4.13395) rot=(0,0,1;0rad)
  Radius = 3.2
  Support = -> [Circle013]
FEATURE [Part::Extrusion] Extrusion041
  Base = -> Circle013
  Dir = (0,0,27.3287)
  DirMode = 0
  FaceMakerClass = Part::FaceMakerBullseye
  LengthFwd = 0
  LengthRev = 0
  Solid = true
  Symmetric = false
FEATURE [Part::Extrusion] Extrusion042
  Base = -> Circle014
  Dir = (0,0,49.2866)
  DirMode = 0
  FaceMakerClass = Part::FaceMakerBullseye
  LengthFwd = 0
  LengthRev = 0
  Solid = true
  Symmetric = false
FEATURE [Part::Cut] Cut010009
  Base = -> Cut010008
  Tool = -> Extrusion041
FEATURE [Part::Cut] Cut010010
  Base = -> Cut010009
  Tool = -> Extrusion042
FEATURE [Part::Part2DObjectPython] Wire004  # Draft 2D object (typed FeaturePython)
  ChamferSize = 0
  Closed = true
  End = (-312.276,-62.7008,1.86605)
  FilletRadius = 0
  Length = 13.6847
  MakeFace = true
  Placement = pos=(-313.776,-62.7008,7.86605) rot=(1,0,0;1.5708rad)
  Points = (3) [(0,0,0),(0,-6,0),(1.5,-6,0)]
  Start = (-313.776,-62.7008,7.86605)
  Subdivisions = 0
FEATURE [Part::Part2DObjectPython] Wire005  # Draft 2D object (typed FeaturePython)
  ChamferSize = 0
  Closed = true
  End = (-312.276,-47.1008,1.86605)
  FilletRadius = 0
  Length = 13.6847
  MakeFace = true
  Placement = pos=(-313.776,-47.1008,7.86605) rot=(1,0,0;1.5708rad)
  Points = (3) [(0,0,0),(0,-6,0),(1.5,-6,0)]
  Start = (-313.776,-47.1008,7.86605)
  Subdivisions = 0
FEATURE [Part::Extrusion] Extrusion043
  Base = -> Wire004
  Dir = (2e-16,6.6,-1.5e-15)
  DirMode = 0
  FaceMakerClass = Part::FaceMakerBullseye
  LengthFwd = 0
  LengthRev = 0
  Solid = true
  Symmetric = false
FEATURE [Part::Extrusion] Extrusion044
  Base = -> Wire005
  Dir = (0,6.6,-1.5e-15)
  DirMode = 0
  FaceMakerClass = Part::FaceMakerBullseye
  LengthFwd = 0
  LengthRev = 0
  Solid = true
  Symmetric = false
FEATURE [Part::MultiFuse] Fusion005002002014004003003002009002010004002
  Shapes = -> [Cut010010,Extrusion043,Extrusion044]
FEATURE [Part::Feature] Fusion005002002014004003003002009002010004002001  label="Fusion005002002014004003003002009002010004003"
  shape: bbox 61.8 x 34.7 x 38.71 mm, 62 faces (baked)
FEATURE [Part::Sphere] Sphere
  Angle1 = -90
  Angle2 = 90
  Angle3 = 360
  AttacherType = Attacher::AttachEngine3D
  Placement = pos=(-309.772,-81.7351,1.86605) rot=(0,0,1;0rad)
  Radius = 1.8
FEATURE [Part::Sphere] Sphere001
  Angle1 = -90
  Angle2 = 90
  Angle3 = 360
  AttacherType = Attacher::AttachEngine3D
  Placement = pos=(-300.84,-81.7351,1.86605) rot=(0,0,1;0rad)
  Radius = 1.8
FEATURE [Part::MultiFuse] Fusion005002002014004003003002009002010004002002
  Shapes = -> [Fusion005002002014004003003002009002010003,Sphere]
FEATURE [Part::MultiFuse] Fusion005002002014004003003002009002010004002003
  Shapes = -> [Fusion005002002014004003003002009002010002,Sphere001]
FEATURE [Part::Feature] Fusion005002002014004003003002009002010004002002001  label="Fusion005002002014004003003002009002010004002004"
  Placement = pos=(0,169.193,-7.1e-15) rot=(0,0,1;0rad)
  shape: bbox 5.6 x 5.6 x 10.8 mm, 5 faces (baked)
FEATURE [Part::Feature] Fusion005002002014004003003002009002010004002003001  label="Fusion005002002014004003003002009002010004002005"
  Placement = pos=(0,169.193,-7.1e-15) rot=(0,0,1;0rad)
  shape: bbox 5.6 x 5.6 x 10.8 mm, 5 faces (baked)
FEATURE [Part::Feature] Fusion005002002014004003003002009002010004002003002  label="Fusion005002002014004003003002009002010004002006"
  shape: bbox 29.42 x 170 x 5.5 mm, 22 faces (baked)
FEATURE [Part::Part2DObjectPython] Polygon  # Draft 2D object (typed FeaturePython)
  ChamferSize = 0
  DrawMode = 0
  FacesNumber = 6
  FilletRadius = 0
  MakeFace = true
  Placement = pos=(-180.455,30.6071,-1.63395) rot=(1,0,0;3.14159rad)
  Radius = 9.2
FEATURE [Part::Part2DObjectPython] Circle015  # Draft 2D object (typed FeaturePython)
  FirstAngle = 0
  LastAngle = 0
  MakeFace = true
  Placement = pos=(-180.455,30.6071,-1.63395) rot=(0,0,1;0rad)
  Radius = 9
  Support = -> [Fusion005002002014004003003002009002010004001]
FEATURE [Part::Extrusion] Extrusion045
  Base = -> Circle015
  Dir = (-2e-15,2.2e-15,-5.5)
  DirMode = 0
  FaceMakerClass = Part::FaceMakerBullseye
  LengthFwd = 0
  LengthRev = 0
  Solid = true
  Symmetric = false
FEATURE [Part::MultiFuse] Fusion005002002014004003003002009002010004002003003
  Shapes = -> [Extrusion045,Fusion005002002014004003003002009002010004001]
FEATURE [Part::Feature] Face010
  Placement = pos=(50.0081,0,-2.22e-14) rot=(0,0,1;0rad)
  shape: bbox 27.5 x 27.42 x 1.743e-06 mm, 1 faces, 0 solids (baked)
FEATURE [Part::Extrusion] Extrusion046
  Base = -> Face010
  Dir = (0,-1.4e-15,2)
  DirMode = 0
  FaceMakerClass = Part::FaceMakerBullseye
  LengthFwd = 0
  LengthRev = 0
  Solid = true
  Symmetric = false
FEATURE [Part::MultiFuse] Fusion005002002014004003003002009002010004002003004
  Shapes = -> [Extrusion046,Fusion005002002014004003003002009002010004002003003]
FEATURE [Part::Extrusion] Extrusion047
  Base = -> Polygon
  Dir = (-1.8e-15,1.2e-15,-4)
  DirMode = 0
  FaceMakerClass = Part::FaceMakerBullseye
  LengthFwd = 0
  LengthRev = 0
  Solid = true
  Symmetric = false
FEATURE [Part::Cut] Cut010011
  Base = -> Fusion005002002014004003003002009002010004002003004
  Tool = -> Extrusion047
FEATURE [Part::Part2DObjectPython] Circle016  # Draft 2D object (typed FeaturePython)
  FirstAngle = 0
  LastAngle = 0
  MakeFace = true
  Placement = pos=(-180.455,30.6071,-7.13395) rot=(1,0,0;3.14159rad)
  Radius = 2.6
  Support = -> [Cut010011]
FEATURE [Part::Extrusion] Extrusion048
  Base = -> Circle016
  Dir = (8.9e-15,-6.2e-15,19.8706)
  DirMode = 0
  FaceMakerClass = Part::FaceMakerBullseye
  LengthFwd = 0
  LengthRev = 0
  Solid = true
  Symmetric = false
FEATURE [Part::Cut] Cut010012
  Base = -> Cut010011
  Tool = -> Extrusion048
FEATURE [Part::Feature] Cut010012001  label="Cut010013"
  shape: bbox 29.42 x 170 x 5.5 mm, 19 faces (baked)
FEATURE [App::DocumentObjectGroup] GrExplode_Slice008  label="Exploded Slice008"
FEATURE [Part::Feature] Face011
  shape: bbox 2 x 28.2 x 1.743e-06 mm, 1 faces, 0 solids (baked)
FEATURE [Part::Extrusion] Extrusion049
  Base = -> Face011
  Dir = (0,0,5.54378)
  DirMode = 0
  FaceMakerClass = Part::FaceMakerBullseye
  LengthFwd = 0
  LengthRev = 0
  Placement = pos=(0,-66.6585,7.5e-14) rot=(0,0,1;0rad)
  Solid = true
  Symmetric = false
FEATURE [Part::Feature] Face012
  Placement = pos=(0,66.6585,-7.5e-14) rot=(0,0,1;0rad)
  shape: bbox 2 x 28.2 x 1.743e-06 mm, 1 faces, 0 solids (baked)
FEATURE [Part::Extrusion] Extrusion050
  Base = -> Face012
  Dir = (0,0,5.54378)
  DirMode = 0
  FaceMakerClass = Part::FaceMakerBullseye
  LengthFwd = 0
  LengthRev = 0
  Placement = pos=(0,-66.377,-0.204339) rot=(0,0,1;0rad)
  Solid = true
  Symmetric = false
FEATURE [Part::MultiFuse] Fusion005002002014004003003002009002010004002003005
  Shapes = -> [Extrusion050,Extrusion049,Fusion005002002014004003003002009002010004002001]
FEATURE [Part::MultiFuse] Fusion005002002014004003003002009002010004002003006
  Placement = pos=(0,51.555,-5.8e-14) rot=(0,0,1;0rad)
  Shapes = -> [Extrusion050,Extrusion049,Fusion005002002014004003003002009002010004002001]
FEATURE [Part::Feature] Fusion005002002014004003003002009002010004002003006001  label="Fusion005002002014004003003002009002010004002003007"
  shape: bbox 61.8 x 34.7 x 38.71 mm, 65 faces (baked)
FEATURE [Part::Part2DObjectPython] Rectangle019  # Draft 2D object (typed FeaturePython)
  ChamferSize = 0
  Columns = 1
  FilletRadius = 0
  Height = 54.4212
  Length = 91.768
  MakeFace = true
  Placement = pos=(-334.423,14.0542,31.0251) rot=(-1,0,0;1.5708rad)
  Rows = 1
  Support = -> [Fusion005002002014004003003002009002010004002003006001]
FEATURE [Part::FeaturePython] Slice008  # WARN: FeaturePython — macro-defined, semantics opaque (R4)
  Base = -> Fusion005002002014004003003002009002010004002003006001
  Mode = 1
  Tolerance = 0
  Tools = -> [Rectangle019]
FEATURE [Part::FeaturePython] Slice008_child0  label="Slice008.0"  # WARN: FeaturePython — macro-defined, semantics opaque (R4)
  Base = -> Slice008
  FilterType = 1
  Invert = false
  OverrideMaxVal = 0
  WindowFrom = 80
  WindowTo = 100
  items = 0
FEATURE [Part::FeaturePython] Slice008_child1  label="Slice008.1"  # WARN: FeaturePython — macro-defined, semantics opaque (R4)
  Base = -> Slice008
  FilterType = 1
  Invert = false
  OverrideMaxVal = 0
  WindowFrom = 80
  WindowTo = 100
  items = 1
FEATURE [Part::FeaturePython] Slice008_child2  label="Slice008.2"  # WARN: FeaturePython — macro-defined, semantics opaque (R4)
  Base = -> Slice008
  FilterType = 1
  Invert = false
  OverrideMaxVal = 0
  WindowFrom = 80
  WindowTo = 100
  items = 2
FEATURE [Part::Part2DObjectPython] Line001  # Draft 2D object (typed FeaturePython)
  ChamferSize = 0
  Closed = false
  End = (-284.876,-14.1458,-7.13395)
  FilletRadius = 0
  Length = 28.2
  MakeFace = true
  Placement = pos=(-284.876,14.0542,-7.13395) rot=(-1,0,0;1.5708rad)
  Points = (2) [(0,0,0),(0,2.04281e-14,-28.2)]
  Start = (-284.876,14.0542,-7.13395)
  Subdivisions = 0
  Support = -> [Slice008_child0]
FEATURE [Part::FeaturePython] Slice008_child003  label="Slice008.003"  # WARN: FeaturePython — macro-defined, semantics opaque (R4)
  Base = -> Slice008
  FilterType = 1
  Invert = false
  OverrideMaxVal = 0
  Placement = pos=(-569.753,-0.0916922,-7e-15) rot=(0,0,1;3.14159rad)
  WindowFrom = 80
  WindowTo = 100
  items = 2
FEATURE [Part::Part2DObjectPython] Line002  # Draft 2D object (typed FeaturePython)
  ChamferSize = 0
  Closed = false
  End = (-284.876,-14.1458,-7.13395)
  FilletRadius = 0
  Length = 28.2
  MakeFace = true
  Placement = pos=(-284.876,14.0542,-7.13395) rot=(-1,0,0;1.5708rad)
  Points = (2) [(0,0,0),(0,2.04281e-14,-28.2)]
  Start = (-284.876,14.0542,-7.13395)
  Subdivisions = 0
  Support = -> [Slice008_child0]
FEATURE [Part::Feature] Fusion005002002014004003003002006003002005003002001  label="Fusion005002002014004003003002006003002005003006008"
  Placement = pos=(-268.233,13.8577,-2) rot=(0,0,1;0rad)
  shape: bbox 26 x 40.3 x 23.5 mm, 48 faces (baked)
FEATURE [Part::Part2DObjectPython] Rectangle020  # Draft 2D object (typed FeaturePython)
  ChamferSize = 0
  Columns = 1
  FilletRadius = 0
  Height = 53.3189
  Length = 64.9539
  MakeFace = true
  Placement = pos=(-393.335,-8.34361,37.566) rot=(-1,0,0;1.5708rad)
  Rows = 1
  Support = -> [Fusion005002002014004003003002006003002005003002001]
FEATURE [Part::FeaturePython] Slice009  # WARN: FeaturePython — macro-defined, semantics opaque (R4)
  Base = -> Fusion005002002014004003003002006003002005003002001
  Mode = 1
  Tolerance = 0
  Tools = -> [Rectangle020]
FEATURE [Part::FeaturePython] Slice009_child0  label="Slice009.0"  # WARN: FeaturePython — macro-defined, semantics opaque (R4)
  Base = -> Slice009
  FilterType = 1
  Invert = false
  OverrideMaxVal = 0
  WindowFrom = 80
  WindowTo = 100
  items = 0
FEATURE [Part::FeaturePython] Slice009_child1  label="Slice009.1"  # WARN: FeaturePython — macro-defined, semantics opaque (R4)
  Base = -> Slice009
  FilterType = 1
  Invert = false
  OverrideMaxVal = 0
  WindowFrom = 80
  WindowTo = 100
  items = 1
FEATURE [Part::FeaturePython] Slice008_child004  label="Slice008.004"  # WARN: FeaturePython — macro-defined, semantics opaque (R4)
  Base = -> Slice008
  FilterType = 1
  Invert = false
  OverrideMaxVal = 0
  Placement = pos=(0,54.2636,-6e-14) rot=(0,0,1;0rad)
  WindowFrom = 80
  WindowTo = 100
  items = 0
FEATURE [Part::Part2DObjectPython] Circle017  # Draft 2D object (typed FeaturePython)
  FirstAngle = 0
  LastAngle = 0
  MakeFace = true
  Placement = pos=(-253.976,54.2177,24.3098) rot=(0.57735,0.57735,0.57735;2.0944rad)
  Radius = 14.1
FEATURE [Part::Part2DObjectPython] Rectangle021  # Draft 2D object (typed FeaturePython)
  ChamferSize = 0
  Columns = 1
  FilletRadius = 0
  Height = 10.9
  Length = 28.2
  MakeFace = true
  Placement = pos=(-253.976,40.1177,13.4098) rot=(0.57735,0.57735,0.57735;2.0944rad)
  Rows = 1
FEATURE [Part::Extrusion] Extrusion051
  Base = -> Rectangle021
  Dir = (-2,0,0)
  DirMode = 0
  FaceMakerClass = Part::FaceMakerBullseye
  LengthFwd = 0
  LengthRev = 0
  Solid = true
  Symmetric = false
FEATURE [Part::Extrusion] Extrusion052
  Base = -> Circle017
  Dir = (-2,0,0)
  DirMode = 0
  FaceMakerClass = Part::FaceMakerBullseye
  LengthFwd = 0
  LengthRev = 0
  Solid = true
  Symmetric = false
FEATURE [Part::MultiFuse] Fusion005002002014004003003002009002010004002003006002
  Shapes = -> [Extrusion052,Extrusion051]
FEATURE [Part::Part2DObjectPython] Rectangle022  # Draft 2D object (typed FeaturePython)
  ChamferSize = 0
  Columns = 1
  FilletRadius = 0
  Height = 23.5
  Length = 26
  MakeFace = true
  Placement = pos=(-365.938,-8.34361,16.3661) rot=(-1,0,0;1.5708rad)
  Rows = 1
  Support = -> [Slice009_child0]
FEATURE [Part::Extrusion] Extrusion053
  Base = -> Rectangle022
  Dir = (-8e-16,-1.39945,-3e-16)
  DirMode = 0
  FaceMakerClass = Part::FaceMakerBullseye
  LengthFwd = 0
  LengthRev = 0
  Solid = true
  Symmetric = false
FEATURE [Part::MultiFuse] Fusion005002002014004003003002009002010004002003006003
  Shapes = -> [Slice009_child0,Extrusion053]
FEATURE [App::DocumentObjectGroup] GrExplode_Slice009  label="Exploded Slice010"
  Group = -> [Slice009_child1,Fusion005002002014004003003002009002010004002003006003]
FEATURE [Part::Feature] Fusion005002002014004003003002009002010004002003006003001  label="Fusion005002002014004003003002009002010004002003006004"
  shape: bbox 26 x 8.799 x 23.5 mm, 34 faces (baked)
FEATURE [Part::Feature] Face013
  shape: bbox 1.943e-06 x 1.399 x 23.5 mm, 1 faces, 0 solids (baked)
FEATURE [Part::Extrusion] Extrusion054
  Base = -> Face013
  Dir = (0.5,0,1e-16)
  DirMode = 0
  FaceMakerClass = Part::FaceMakerBullseye
  LengthFwd = 0
  LengthRev = 0
  Solid = true
  Symmetric = false
FEATURE [Part::MultiFuse] Fusion005002002014004003003002009002010004002003006003002
  Shapes = -> [Fusion005002002014004003003002009002010004002003006003001,Extrusion054]
FEATURE [Part::Part2DObjectPython] Rectangle023  # Draft 2D object (typed FeaturePython)
  ChamferSize = 0
  Columns = 1
  FilletRadius = 0
  Height = 23.9953
  Length = 15
  MakeFace = true
  Placement = pos=(-339.438,-23.3436,-7.62923) rot=(0.57735,0.57735,0.57735;2.0944rad)
  Rows = 1
FEATURE [Part::Part2DObjectPython] Circle018  # Draft 2D object (typed FeaturePython)
  FirstAngle = 0
  LastAngle = 0
  MakeFace = true
  Placement = pos=(-339.438,-23.3436,4.36841) rot=(0.57735,0.57735,0.57735;2.0944rad)
  Radius = 11.9976
FEATURE [Part::Extrusion] Extrusion055
  Base = -> Rectangle023
  Dir = (1.5,-2e-15,-2e-15)
  DirMode = 0
  FaceMakerClass = Part::FaceMakerBullseye
  LengthFwd = 0
  LengthRev = 0
  Solid = true
  Symmetric = false
FEATURE [Part::Extrusion] Extrusion056
  Base = -> Circle018
  Dir = (1.5,-2e-15,-2e-15)
  DirMode = 0
  FaceMakerClass = Part::FaceMakerBullseye
  LengthFwd = 0
  LengthRev = 0
  Solid = true
  Symmetric = false
FEATURE [Part::MultiFuse] Fusion005002002014004003003002009002010004002003006003003
  Shapes = -> [Extrusion056,Extrusion055]
FEATURE [Part::Part2DObjectPython] Circle019  # Draft 2D object (typed FeaturePython)
  FirstAngle = 0
  LastAngle = 0
  MakeFace = true
  Placement = pos=(-339.438,-23.3436,4.36841) rot=(0.57735,-0.57735,-0.57735;2.0944rad)
  Radius = 0.5
FEATURE [Part::Extrusion] Extrusion057
  Base = -> Circle019
  Dir = (41.562,0,0)
  DirMode = 0
  FaceMakerClass = Part::FaceMakerBullseye
  LengthFwd = 0
  LengthRev = 0
  Solid = true
  Symmetric = false
FEATURE [Part::Cut] Cut010012002
  Base = -> Fusion005002002014004003003002009002010004002003006003003
  Tool = -> Extrusion057
FEATURE [Part::Part2DObjectPython] Circle020  # Draft 2D object (typed FeaturePython)
  FirstAngle = 0
  LastAngle = 0
  MakeFace = true
  Placement = pos=(-255.976,54.2177,24.3098) rot=(0.57735,-0.57735,-0.57735;2.0944rad)
  Radius = 0.7
  Support = -> [Fusion005002002014004003003002009002010004002003006002]
FEATURE [Part::Extrusion] Extrusion058
  Base = -> Circle020
  Dir = (27.4294,0,0)
  DirMode = 0
  FaceMakerClass = Part::FaceMakerBullseye
  LengthFwd = 0
  LengthRev = 0
  Solid = true
  Symmetric = false
FEATURE [Part::Cut] Cut010012003
  Base = -> Fusion005002002014004003003002009002010004002003006002
  Tool = -> Extrusion058
FEATURE [Part::MultiFuse] Fusion005002002014004003003002009002010004002003006003004
  Shapes = -> [Slice008_child004,Cut010012003]
FEATURE [Part::MultiFuse] Fusion005002002014004003003002009002010004002003006003005
  Placement = pos=(85.4841,111.471,-2.1e-14) rot=(0,0,1;0rad)
  Shapes = -> [Fusion005002002014004003003002009002010004002003006003002,Cut010012002]
FEATURE [Part::Part2DObjectPython] Rectangle024  # Draft 2D object (typed FeaturePython)
  ChamferSize = 0
  Columns = 1
  FilletRadius = 0
  Height = 53.283
  Length = 35.4242
  MakeFace = true
  Placement = pos=(-253.954,109.095,-27.9814) rot=(0.57735,-0.57735,-0.57735;2.0944rad)
  Rows = 1
  Support = -> [Fusion005002002014004003003002009002010004002003006003005]
FEATURE [Part::FeaturePython] Slice010  # WARN: FeaturePython — macro-defined, semantics opaque (R4)
  Base = -> Fusion005002002014004003003002009002010004002003006003005
  Mode = 1
  Tolerance = 0
  Tools = -> [Rectangle024]
FEATURE [Part::FeaturePython] Slice010_child0  label="Slice010.0"  # WARN: FeaturePython — macro-defined, semantics opaque (R4)
  Base = -> Slice010
  FilterType = 1
  Invert = false
  OverrideMaxVal = 0
  WindowFrom = 80
  WindowTo = 100
  items = 0
FEATURE [Part::FeaturePython] Slice010_child1  label="Slice010.1"  # WARN: FeaturePython — macro-defined, semantics opaque (R4)
  Base = -> Slice010
  FilterType = 1
  Invert = false
  OverrideMaxVal = 0
  Placement = pos=(0,-10,0) rot=(0,0,1;0rad)
  WindowFrom = 80
  WindowTo = 100
  items = 1
FEATURE [Part::Feature] Face014
  Placement = pos=(0,-10,0) rot=(0,0,1;0rad)
  shape: bbox 1.5 x 1.943e-06 x 24 mm, 1 faces, 0 solids (baked)
FEATURE [Part::Extrusion] Extrusion059
  Base = -> Face014
  Dir = (1.33e-14,10,1.33e-14)
  DirMode = 0
  FaceMakerClass = Part::FaceMakerBullseye
  LengthFwd = 0
  LengthRev = 0
  Solid = true
  Symmetric = false
FEATURE [Part::MultiFuse] Fusion005002002014004003003002009002010004002003006003006
  Shapes = -> [Slice010_child1,Extrusion059]
FEATURE [Part::MultiFuse] Fusion005002002014004003003002009002010004002003006003007
  Placement = pos=(-34.6371,6.22765,6.2e-15) rot=(0,0,1;0rad)
  Shapes = -> [Fusion005002002014004003003002009002010004002003006003006,Slice010_child0]
FEATURE [App::DocumentObjectGroup] GrExplode_Slice010  label="Exploded Slice011"
  Group = -> [Fusion005002002014004003003002009002010004002003006003007]
FEATURE [Part::Feature] Face015
  Placement = pos=(0,105.819,-1.181e-13) rot=(0,0,1;0rad)
  shape: bbox 2 x 1.843e-06 x 5.339 mm, 1 faces, 0 solids (baked)
FEATURE [Part::Extrusion] Extrusion060
  Base = -> Face015
  Dir = (0,-0.281515,0)
  DirMode = 0
  FaceMakerClass = Part::FaceMakerBullseye
  LengthFwd = 0
  LengthRev = 0
  Solid = true
  Symmetric = false
FEATURE [Part::MultiFuse] Fusion005002002014004003003002009002010004002003006003008
  Shapes = -> [Fusion005002002014004003003002009002010004002003006003004,Extrusion060]
FEATURE [Part::Feature] Fusion005002002014004003003002009002010004002003006003008001  label="Fusion005002002014004003003002009002010004002003006003009"
  shape: bbox 61.8 x 28.2 x 45.54 mm, 51 faces (baked)
FEATURE [Part::Feature] Face016
  Placement = pos=(-309.772,87.4582,-7.13395) rot=(1,0,0;3.14159rad)
  shape: bbox 5.6 x 5.6 x 2e-07 mm, 1 faces, 0 solids (baked)
FEATURE [Part::Extrusion] Extrusion061
  Base = -> Face016
  Dir = (0,1e-15,1)
  DirMode = 0
  FaceMakerClass = Part::FaceMakerBullseye
  LengthFwd = 0
  LengthRev = 0
  Solid = true
  Symmetric = false
FEATURE [Part::Feature] Face017
  Placement = pos=(-300.84,87.4582,-7.13395) rot=(1,0,0;3.14159rad)
  shape: bbox 5.6 x 5.6 x 2e-07 mm, 1 faces, 0 solids (baked)
FEATURE [Part::Extrusion] Extrusion062
  Base = -> Face017
  Dir = (0,1e-15,1)
  DirMode = 0
  FaceMakerClass = Part::FaceMakerBullseye
  LengthFwd = 0
  LengthRev = 0
  Solid = true
  Symmetric = false
FEATURE [Part::Cut] Cut010012004
  Base = -> Fusion005002002014004003003002009002010004002002001
  Tool = -> Extrusion061
FEATURE [Part::Cut] Cut010012005
  Base = -> Fusion005002002014004003003002009002010004002003001
  Tool = -> Extrusion062
FEATURE [Part::Part2DObjectPython] Rectangle025  # Draft 2D object (typed FeaturePython)
  ChamferSize = 0
  Columns = 1
  FilletRadius = 0
  Height = 10.2957
  Length = 9.75222
  MakeFace = true
  Placement = pos=(-312.848,82.3103,-0.133948) rot=(0,0,1;0rad)
  Rows = 1
  Support = -> [Fusion005002002014004003003002009002010004002003006003007]
FEATURE [Part::FeaturePython] Slice011  # WARN: FeaturePython — macro-defined, semantics opaque (R4)
  Base = -> Cut010012004
  Mode = 1
  Tolerance = 0
  Tools = -> [Rectangle025]
FEATURE [Part::FeaturePython] Slice011_child0  label="Slice011.0"  # WARN: FeaturePython — macro-defined, semantics opaque (R4)
  Base = -> Slice011
  FilterType = 1
  Invert = false
  OverrideMaxVal = 0
  WindowFrom = 80
  WindowTo = 100
  items = 0
FEATURE [App::DocumentObjectGroup] GrExplode_Slice011  label="Exploded Slice012"
  Group = -> [Slice011_child0]
FEATURE [Part::FeaturePython] Slice011_child1  label="Slice011.1"  # WARN: FeaturePython — macro-defined, semantics opaque (R4)
  Base = -> Slice011
  FilterType = 1
  Invert = false
  OverrideMaxVal = 0
  WindowFrom = 80
  WindowTo = 100
  items = 1
FEATURE [Part::Part2DObjectPython] Rectangle026  # Draft 2D object (typed FeaturePython)
  ChamferSize = 0
  Columns = 1
  FilletRadius = 0
  Height = 9.15406
  Length = 8.92824
  MakeFace = true
  Placement = pos=(-312.436,82.8812,1.86605) rot=(0,0,1;0rad)
  Rows = 1
FEATURE [Part::FeaturePython] Slice012  # WARN: FeaturePython — macro-defined, semantics opaque (R4)
  Base = -> Slice011_child0
  Mode = 1
  Tolerance = 0
  Tools = -> [Rectangle026]
FEATURE [Part::FeaturePython] Slice012_child0  label="Slice012.0"  # WARN: FeaturePython — macro-defined, semantics opaque (R4)
  Base = -> Slice012
  FilterType = 1
  Invert = false
  OverrideMaxVal = 0
  Placement = pos=(0,0,-2) rot=(0,0,1;0rad)
  WindowFrom = 80
  WindowTo = 100
  items = 0
FEATURE [Part::Part2DObjectPython] Rectangle027  # Draft 2D object (typed FeaturePython)
  ChamferSize = 0
  Columns = 1
  FilletRadius = 0
  Height = 8.96913
  Length = 9.30222
  MakeFace = true
  Placement = pos=(-303.691,82.9736,1.86605) rot=(0,0,1;0rad)
  Rows = 1
FEATURE [Part::FeaturePython] Slice013  # WARN: FeaturePython — macro-defined, semantics opaque (R4)
  Base = -> Cut010012005
  Mode = 1
  Tolerance = 0
  Tools = -> [Rectangle027]
FEATURE [Part::FeaturePython] Slice013_child0  label="Slice013.0"  # WARN: FeaturePython — macro-defined, semantics opaque (R4)
  Base = -> Slice013
  FilterType = 1
  Invert = false
  OverrideMaxVal = 0
  Placement = pos=(0,0,-2) rot=(0,0,1;0rad)
  WindowFrom = 80
  WindowTo = 100
  items = 0
FEATURE [Part::FeaturePython] Slice013_child1  label="Slice013.1"  # WARN: FeaturePython — macro-defined, semantics opaque (R4)
  Base = -> Slice013
  FilterType = 1
  Invert = false
  OverrideMaxVal = 0
  WindowFrom = 80
  WindowTo = 100
  items = 1
FEATURE [Part::Part2DObjectPython] Rectangle028  # Draft 2D object (typed FeaturePython)
  ChamferSize = 0
  Columns = 1
  FilletRadius = 0
  Height = 12.5844
  Length = 22.5249
  MakeFace = true
  Placement = pos=(-307.972,81.166,-0.133948) rot=(0,0,1;0rad)
  Rows = 1
FEATURE [Part::FeaturePython] Slice014  # WARN: FeaturePython — macro-defined, semantics opaque (R4)
  Base = -> Slice013_child1
  Mode = 1
  Tolerance = 0
  Tools = -> [Rectangle028]
FEATURE [App::DocumentObjectGroup] GrExplode_Slice014  label="Exploded Slice015"
FEATURE [Part::FeaturePython] Slice014_child0  label="Slice014.0"  # WARN: FeaturePython — macro-defined, semantics opaque (R4)
  Base = -> Slice014
  FilterType = 1
  Invert = false
  OverrideMaxVal = 0
  WindowFrom = 80
  WindowTo = 100
  items = 0
FEATURE [Part::MultiFuse] Fusion005002002014004003003002009002010004002003006003008002
  Placement = pos=(43.4001,56.4769,-1) rot=(0,0,1;0rad)
  Shapes = -> [Slice014_child0,Slice013_child0]
FEATURE [App::DocumentObjectGroup] GrExplode_Slice013  label="Exploded Slice014"
  Group = -> [Slice013_child1,Fusion005002002014004003003002009002010004002003006003008002]
FEATURE [Part::MultiFuse] Fusion005002002014004003003002009002010004002003006003008003
  Placement = pos=(43.027,56.4637,-1) rot=(0,0,1;0rad)
  Shapes = -> [Slice011_child1,Slice012_child0]
FEATURE [App::DocumentObjectGroup] GrExplode_Slice012  label="Exploded Slice013"
  Group = -> [Fusion005002002014004003003002009002010004002003006003008003]
FEATURE [Part::Feature] Face018
  Placement = pos=(-304.776,46.6177,0.366052) rot=(0,0,1;0rad)
  shape: bbox 3 x 15.2 x 2e-07 mm, 1 faces, 0 solids (baked)
FEATURE [Part::Extrusion] Extrusion063
  Base = -> Face018
  Dir = (0,0,-0.5)
  DirMode = 0
  FaceMakerClass = Part::FaceMakerBullseye
  LengthFwd = 0
  LengthRev = 0
  Solid = true
  Symmetric = false
FEATURE [Part::Cut] Cut010012006
  Base = -> Fusion005002002014004003003002009002010004002003006003008001
  Placement = pos=(0,163.645,-1.83e-13) rot=(0,0,1;0rad)
  Tool = -> Extrusion063
FEATURE [Part::Feature] Face019
  Placement = pos=(-304.776,-7.64585,0.366052) rot=(0,0,1;0rad)
  shape: bbox 3 x 15.2 x 2e-07 mm, 1 faces, 0 solids (baked)
FEATURE [Part::Extrusion] Extrusion064
  Base = -> Face019
  Dir = (0,0,-0.5)
  DirMode = 0
  FaceMakerClass = Part::FaceMakerBullseye
  LengthFwd = 0
  LengthRev = 0
  Solid = true
  Symmetric = false
FEATURE [Part::Feature] Face020
  Placement = pos=(-304.776,-59.2008,0.366052) rot=(0,0,1;0rad)
  shape: bbox 3 x 15.2 x 2e-07 mm, 1 faces, 0 solids (baked)
FEATURE [Part::Extrusion] Extrusion065
  Base = -> Face020
  Dir = (0,0,-0.5)
  DirMode = 0
  FaceMakerClass = Part::FaceMakerBullseye
  LengthFwd = 0
  LengthRev = 0
  Solid = true
  Symmetric = false
FEATURE [Part::Cut] Cut010012007
  Base = -> Fusion005002002014004003003002009002010004002003005
  Tool = -> Extrusion065
FEATURE [Part::Cut] Cut010012008
  Base = -> Slice008_child0
  Tool = -> Extrusion064
FEATURE [App::DocumentObjectGroup] GrExplode_Slice008001  label="Exploded Slice009"
  Group = -> [Slice008_child1,Slice008_child2,Cut010012008]
FEATURE [Part::Feature] Face021
  Placement = pos=(50.847,117.698,-1.51e-14) rot=(0,0,1;0rad)
  shape: bbox 2.043e-06 x 1.399 x 23.5 mm, 1 faces, 0 solids (baked)
FEATURE [Part::Feature] Face022
  Placement = pos=(50.847,117.698,-1.51e-14) rot=(0,0,1;0rad)
  shape: bbox 2.043e-06 x 1.399 x 23.5 mm, 1 faces, 0 solids (baked)
FEATURE [Part::MultiFuse] Fusion005002002014004003003002009002010004002003006003008004
  Placement = pos=(-34.6371,55.2721,4e-15) rot=(0,0,1;0rad)
  Shapes = -> [Fusion005002002014004003003002009002010004002003006003006,Slice010_child0]
FEATURE [Part::Feature] Face023
  Placement = pos=(50.847,166.743,-1.7e-14) rot=(0,0,1;0rad)
  shape: bbox 2.043e-06 x 1.399 x 23.5 mm, 1 faces, 0 solids (baked)
FEATURE [Part::Extrusion] Extrusion066
  Base = -> Face023
  Dir = (-0.487131,0,-1e-16)
  DirMode = 0
  FaceMakerClass = Part::FaceMakerBullseye
  LengthFwd = 0
  LengthRev = 0
  Solid = true
  Symmetric = false
FEATURE [Part::Part2DObjectPython] Rectangle029  # Draft 2D object (typed FeaturePython)
  ChamferSize = 0
  Columns = 1
  FilletRadius = 0
  Height = 144.729
  Length = 71.3289
  MakeFace = true
  Placement = pos=(-288.591,186.93,-88.9388) rot=(0.57735,-0.57735,-0.57735;2.0944rad)
  Rows = 1
  Support = -> [Fusion005002002014004003003002009002010004002003006003008004]
FEATURE [Part::FeaturePython] Slice015  # WARN: FeaturePython — macro-defined, semantics opaque (R4)
  Base = -> Fusion005002002014004003003002009002010004002003006003008004
  Mode = 1
  Tolerance = 0
  Tools = -> [Rectangle029]
FEATURE [Part::FeaturePython] Slice015_child0  label="Slice015.0"  # WARN: FeaturePython — macro-defined, semantics opaque (R4)
  Base = -> Slice015
  FilterType = 1
  Invert = false
  OverrideMaxVal = 0
  WindowFrom = 80
  WindowTo = 100
  items = 0
FEATURE [Part::FeaturePython] Slice015_child1  label="Slice015.1"  # WARN: FeaturePython — macro-defined, semantics opaque (R4)
  Base = -> Slice015
  FilterType = 1
  Invert = false
  OverrideMaxVal = 0
  Placement = pos=(-577.182,316.798,1.19e-12) rot=(0,0,1;3.14159rad)
  WindowFrom = 80
  WindowTo = 100
  items = 1
FEATURE [Part::Cut] Cut010012009
  Base = -> Fusion005002002014004003003002009002010004002003006003008001
  Tool = -> Extrusion063
FEATURE [Part::Part2DObjectPython] Rectangle030  # Draft 2D object (typed FeaturePython)
  ChamferSize = 0
  Columns = 1
  FilletRadius = 0
  Height = 2
  Length = 40.3882
  MakeFace = true
  Placement = pos=(-294.364,233.963,-7.13395) rot=(1,0,0;3.14159rad)
  Rows = 1
FEATURE [Part::Extrusion] Extrusion067
  Base = -> Rectangle030
  Dir = (6e-16,2.28e-14,20.3394)
  DirMode = 0
  FaceMakerClass = Part::FaceMakerBullseye
  LengthFwd = 0
  LengthRev = 0
  Solid = true
  Symmetric = false
FEATURE [Part::Extrusion] Extrusion068
  Base = -> Rectangle030
  Dir = (6e-16,2.28e-14,20.3394)
  DirMode = 0
  FaceMakerClass = Part::FaceMakerBullseye
  LengthFwd = 0
  LengthRev = 0
  Placement = pos=(0,-30.2,3e-15) rot=(0,0,1;0rad)
  Solid = true
  Symmetric = false
FEATURE [Part::Part2DObjectPython] Rectangle031  # Draft 2D object (typed FeaturePython)
  ChamferSize = 0
  Columns = 1
  FilletRadius = 0
  Height = 29.3616
  Length = 55.1531
  MakeFace = true
  Placement = pos=(-270.396,237.734,13.2055) rot=(0,0,-1;1.5708rad)
  Rows = 1
  Support = -> [Extrusion068]
FEATURE [Part::FeaturePython] Slice016  # WARN: FeaturePython — macro-defined, semantics opaque (R4)
  Base = -> Cut010012006
  Mode = 1
  Tolerance = 0
  Tools = -> [Rectangle031]
FEATURE [App::DocumentObjectGroup] GrExplode_Slice016  label="Exploded Slice017"
FEATURE [Part::FeaturePython] Slice016_child0  label="Slice016.0"  # WARN: FeaturePython — macro-defined, semantics opaque (R4)
  Base = -> Slice016
  FilterType = 1
  Invert = false
  OverrideMaxVal = 0
  WindowFrom = 80
  WindowTo = 100
  items = 0
FEATURE [Part::Part2DObjectPython] Rectangle032  # Draft 2D object (typed FeaturePython)
  ChamferSize = 0
  Columns = 1
  FilletRadius = 0
  Height = 1.3
  Length = 1.3
  MakeFace = true
  Placement = pos=(-313.776,231.963,-1.83395) rot=(-1,0,0;1.5708rad)
  Rows = 1
  Support = -> [Slice016_child0]
FEATURE [Part::Extrusion] Extrusion069
  Base = -> Rectangle032
  Dir = (-7.3e-15,-28.2,1.25e-14)
  DirMode = 0
  FaceMakerClass = Part::FaceMakerBullseye
  LengthFwd = 0
  LengthRev = 0
  Solid = true
  Symmetric = false
FEATURE [Part::Part2DObjectPython] Circle021  # Draft 2D object (typed FeaturePython)
  FirstAngle = 0
  LastAngle = 0
  MakeFace = true
  Placement = pos=(-312.476,231.963,-1.83395) rot=(-1,0,0;1.5708rad)
  Radius = 1.3
  Support = -> [Extrusion069]
FEATURE [Part::Extrusion] Extrusion070
  Base = -> Circle021
  Dir = (-3.6e-15,-28.2,6.3e-15)
  DirMode = 0
  FaceMakerClass = Part::FaceMakerBullseye
  LengthFwd = 0
  LengthRev = 0
  Solid = true
  Symmetric = false
FEATURE [Part::Cut] Cut010012010
  Base = -> Extrusion069
  Tool = -> Extrusion070
FEATURE [Part::Part2DObjectPython] Rectangle033  # Draft 2D object (typed FeaturePython)
  ChamferSize = 0
  Columns = 1
  FilletRadius = 0
  Height = 45.8705
  Length = 32.4772
  MakeFace = true
  Placement = pos=(-273.853,183.399,-18.0668) rot=(0,0.707107,0.707107;3.14159rad)
  Rows = 1
  Support = -> [Slice015_child0]
FEATURE [Part::FeaturePython] Slice017  # WARN: FeaturePython — macro-defined, semantics opaque (R4)
  Base = -> Slice015_child1
  Mode = 1
  Tolerance = 0
  Tools = -> [Rectangle033]
FEATURE [Part::FeaturePython] Slice017_child0  label="Slice017.0"  # WARN: FeaturePython — macro-defined, semantics opaque (R4)
  Base = -> Slice017
  FilterType = 1
  Invert = false
  OverrideMaxVal = 0
  WindowFrom = 80
  WindowTo = 100
  items = 0
FEATURE [App::DocumentObjectGroup] GrExplode_Slice017  label="Exploded Slice018"
  Group = -> [Slice017_child0]
FEATURE [Part::Part2DObjectPython] Rectangle034  # Draft 2D object (typed FeaturePython)
  ChamferSize = 0
  Columns = 1
  FilletRadius = 0
  Height = 73.2019
  Length = 7.52448
  MakeFace = true
  Placement = pos=(-286.329,168.399,-20.2349) rot=(0,0.707107,0.707107;3.14159rad)
  Rows = 1
  Support = -> [Slice015_child0]
FEATURE [Part::FeaturePython] Slice018  # WARN: FeaturePython — macro-defined, semantics opaque (R4)
  Base = -> Slice017_child0
  Mode = 1
  Tolerance = 0
  Tools = -> [Rectangle034]
FEATURE [App::DocumentObjectGroup] GrExplode_Slice018  label="Exploded Slice019"
FEATURE [Part::FeaturePython] Slice018_child0  label="Slice018.0"  # WARN: FeaturePython — macro-defined, semantics opaque (R4)
  Base = -> Slice018
  FilterType = 1
  Invert = false
  OverrideMaxVal = 0
  Placement = pos=(1.5,-10,-2.1e-14) rot=(0,0,1;0rad)
  WindowFrom = 80
  WindowTo = 100
  items = 0
FEATURE [Part::Feature] Face024
  Placement = pos=(-575.682,306.798,1.169e-12) rot=(0,0,1;3.14159rad)
  shape: bbox 1.5 x 1.943e-06 x 24 mm, 1 faces, 0 solids (baked)
FEATURE [Part::Extrusion] Extrusion071
  Base = -> Face024
  Dir = (-2.82e-14,-19.3995,-2.58e-14)
  DirMode = 0
  FaceMakerClass = Part::FaceMakerBullseye
  LengthFwd = 0
  LengthRev = 0
  Solid = true
  Symmetric = false
FEATURE [Part::MultiFuse] Fusion005002002014004003003002009002010004002003006003008006
  Shapes = -> [Extrusion071,Slice018_child0]
FEATURE [Part::MultiFuse] Fusion005002002014004003003002009002010004002003006003008007
  Placement = pos=(-28.4871,-2.8e-14,0) rot=(0,0,1;0rad)
  Shapes = -> [Extrusion071,Slice018_child0]
FEATURE [Part::MultiFuse] Fusion005002002014004003003002009002010004002003006003008008
  Shapes = -> [Fusion005002002014004003003002009002010004002003006003008007,Fusion005002002014004003003002009002010004002003006003008006,Slice015_child0]
FEATURE [App::DocumentObjectGroup] GrExplode_Slice015  label="Exploded Slice016"
  Group = -> [Slice015_child1,Fusion005002002014004003003002009002010004002003006003008008]
FEATURE [Part::Feature] Fusion005002002014004003003002009002010004002003006003008008001  label="Fusion005002002014004003003002009002010004002003006003008009"
  shape: bbox 29.99 x 29.4 x 24 mm, 43 faces, 2 solids (baked)
FEATURE [Part::Feature] Face025
  shape: bbox 1.5 x 29.4 x 4.243e-07 mm, 1 faces, 0 solids (baked)
FEATURE [Part::Extrusion] Extrusion072
  Base = -> Face025
  Dir = (-1.15e-14,-2.01e-14,-8.20472)
  DirMode = 0
  FaceMakerClass = Part::FaceMakerBullseye
  LengthFwd = 0
  LengthRev = 0
  Solid = true
  Symmetric = false
FEATURE [Part::Feature] Face026
  shape: bbox 1.5 x 29.4 x 2.065e-06 mm, 1 faces, 0 solids (baked)
FEATURE [Part::Extrusion] Extrusion073
  Base = -> Face026
  Dir = (-1e-14,1.09e-14,-8.20472)
  DirMode = 0
  FaceMakerClass = Part::FaceMakerBullseye
  LengthFwd = 0
  LengthRev = 0
  Solid = true
  Symmetric = false
FEATURE [Part::Feature] Face027
  shape: bbox 26.5 x 8.799 x 2.065e-06 mm, 1 faces, 0 solids (baked)
FEATURE [Part::Extrusion] Extrusion074
  Base = -> Face027
  Dir = (-5e-16,-2.5e-15,-8.7)
  DirMode = 0
  FaceMakerClass = Part::FaceMakerBullseye
  LengthFwd = 0
  LengthRev = 0
  Solid = true
  Symmetric = false
FEATURE [Part::Feature] Face028
  shape: bbox 0.4871 x 1.399 x 2.043e-06 mm, 1 faces, 0 solids (baked)
FEATURE [Part::Extrusion] Extrusion075
  Base = -> Face028
  Dir = (1.1e-15,2.7e-15,-8.7)
  DirMode = 0
  FaceMakerClass = Part::FaceMakerBullseye
  LengthFwd = 0
  LengthRev = 0
  Solid = true
  Symmetric = false
FEATURE [Part::MultiFuse] Fusion005002002014004003003002009002010004002003006003008008002
  Shapes = -> [Fusion005002002014004003003002009002010004002003006003008008001,Extrusion073,Extrusion072]
FEATURE [Part::MultiFuse] Fusion005002002014004003003002009002010004002003006003008008003
  Shapes = -> [Fusion005002002014004003003002009002010004002003006003008008002,Extrusion074]
FEATURE [Part::MultiFuse] Fusion005002002014004003003002009002010004002003006003008008004
  Shapes = -> [Fusion005002002014004003003002009002010004002003006003008008003,Extrusion075]
FEATURE [Part::Feature] Fusion005002002014004003003002009002010004002003006003008008004001  label="Fusion005002002014004003003002009002010004002003006003008008005"
  shape: bbox 29.99 x 29.4 x 32.2 mm, 41 faces (baked)
FEATURE [Part::Part2DObjectPython] Circle022  # Draft 2D object (typed FeaturePython)
  FirstAngle = 0
  LastAngle = 0
  MakeFace = true
  Placement = pos=(-315.578,158.399,0.266052) rot=(-0.57735,0.57735,0.57735;4.18879rad)
  Radius = 16.1
  Support = -> [Fusion005002002014004003003002009002010004002003006003008008004001]
FEATURE [Part::Part2DObjectPython] Polygon001  # Draft 2D object (typed FeaturePython)
  ChamferSize = 0
  DrawMode = 0
  FacesNumber = 6
  FilletRadius = 0
  MakeFace = true
  Placement = pos=(-315.578,162.037,0.266052) rot=(0.707107,0,-0.707107;3.14159rad)
  Radius = 4.2
FEATURE [Part::MultiFuse] Fusion005002002014004003003002009002010004002003006003008008004002
  Shapes = -> [Fusion005002002014004003003002009002010004002003006003008008004001,Extrusion066]
FEATURE [Part::Extrusion] Extrusion076
  Base = -> Polygon001
  Dir = (28.4871,0,6.3e-15)
  DirMode = 0
  FaceMakerClass = Part::FaceMakerBullseye
  LengthFwd = 0
  LengthRev = 0
  Solid = true
  Symmetric = false
FEATURE [Part::Extrusion] Extrusion077
  Base = -> Circle022
  Dir = (3.4,-1.21e-14,-1.13e-14)
  DirMode = 0
  FaceMakerClass = Part::FaceMakerBullseye
  LengthFwd = 0
  LengthRev = 0
  Solid = true
  Symmetric = false
FEATURE [Part::Cut] Cut010012011
  Base = -> Extrusion077
  Tool = -> Extrusion076
FEATURE [Part::Part2DObjectPython] Rectangle035  # Draft 2D object (typed FeaturePython)
  ChamferSize = 0
  Columns = 1
  FilletRadius = 0
  Height = 77.9235
  Length = 30.563
  MakeFace = true
  Placement = pos=(-332.163,158.399,26.3796) rot=(-1,0,0;1.5708rad)
  Rows = 1
  Support = -> [Fusion005002002014004003003002009002010004002003006003008008004002]
FEATURE [Part::FeaturePython] Slice019  # WARN: FeaturePython — macro-defined, semantics opaque (R4)
  Base = -> Cut010012011
  Mode = 1
  Tolerance = 0
  Tools = -> [Rectangle035]
FEATURE [App::DocumentObjectGroup] GrExplode_Slice019  label="Exploded Slice020"
FEATURE [Part::Feature] Face029
  shape: bbox 3e-07 x 16.1 x 32.2 mm, 1 faces, 0 solids (baked)
FEATURE [Part::Part2DObjectPython] Wire006  # Draft 2D object (typed FeaturePython)
  ChamferSize = 0
  Closed = true
  End = (-317.078,158.399,2.36605)
  FilletRadius = 0
  Length = 25.2
  MakeFace = true
  Placement = pos=(-317.078,158.399,-1.83395) rot=(0.57735,-0.57735,-0.57735;2.0944rad)
  Points = (6) [(0,0,0),(-3.63731,-2.1,5.68434e-14),(-7.27461,-8.43769e-15,5.68434e-14),(-7.27461,4.2,5.68434e-14),(-3.63731,6.3,5.68434e-14),(0,4.2,0)]
  Start = (-317.078,158.399,-1.83395)
  Subdivisions = 0
FEATURE [Part::Extrusion] Extrusion079
  Base = -> Wire006
  Dir = (1.5,1.17e-14,0)
  DirMode = 0
  FaceMakerClass = Part::FaceMakerBullseye
  LengthFwd = 0
  LengthRev = 0
  Solid = true
  Symmetric = false
FEATURE [Part::Part2DObjectPython] Circle023  # Draft 2D object (typed FeaturePython)
  FirstAngle = 0
  LastAngle = 0
  MakeFace = true
  Placement = pos=(-317.078,162.037,0.266052) rot=(0.57735,-0.57735,-0.57735;2.0944rad)
  Radius = 2.2
FEATURE [Part::Extrusion] Extrusion080
  Base = -> Circle023
  Dir = (24.9014,0,0)
  DirMode = 0
  FaceMakerClass = Part::FaceMakerBullseye
  LengthFwd = 0
  LengthRev = 0
  Solid = true
  Symmetric = false
FEATURE [Part::Cut] Cut010012012
  Base = -> Extrusion079
  Tool = -> Extrusion080
FEATURE [Part::Part2DObjectPython] Circle024  # Draft 2D object (typed FeaturePython)
  FirstAngle = 0
  LastAngle = 0
  MakeFace = true
  Placement = pos=(-317.078,162.037,0.266052) rot=(0.57735,-0.57735,-0.57735;2.0944rad)
  Radius = 16.1
  Support = -> [Cut010012012]
FEATURE [Part::Extrusion] Extrusion081
  Base = -> Circle024
  Dir = (1.5,0,0)
  DirMode = 0
  FaceMakerClass = Part::FaceMakerBullseye
  LengthFwd = 0
  LengthRev = 0
  Solid = true
  Symmetric = false
FEATURE [Part::Feature] Face030
  shape: bbox 2e-07 x 7.275 x 8.4 mm, 1 faces, 0 solids (baked)
FEATURE [Part::Extrusion] Extrusion082
  Base = -> Face030
  Dir = (31.5425,2.465e-13,0)
  DirMode = 0
  FaceMakerClass = Part::FaceMakerBullseye
  LengthFwd = 0
  LengthRev = 0
  Solid = true
  Symmetric = false
FEATURE [Part::Feature] Face031
  Placement = pos=(-315.578,162.037,0.266052) rot=(0.57735,-0.57735,-0.57735;2.0944rad)
  shape: bbox 2e-07 x 32.2 x 32.2 mm, 1 faces, 0 solids (baked)
FEATURE [Part::Extrusion] Extrusion083
  Base = -> Face031
  Dir = (3.4,0,0)
  DirMode = 0
  FaceMakerClass = Part::FaceMakerBullseye
  LengthFwd = 0
  LengthRev = 0
  Solid = true
  Symmetric = false
FEATURE [Part::Part2DObjectPython] Rectangle036  # Draft 2D object (typed FeaturePython)
  ChamferSize = 0
  Columns = 1
  FilletRadius = 0
  Height = 71.6631
  Length = 82.5883
  MakeFace = true
  Placement = pos=(-341.676,158.399,38.2563) rot=(-1,0,0;1.5708rad)
  Rows = 1
FEATURE [Part::FeaturePython] Slice020  # WARN: FeaturePython — macro-defined, semantics opaque (R4)
  Base = -> Extrusion083
  Mode = 1
  Tolerance = 0
  Tools = -> [Rectangle036]
FEATURE [Part::FeaturePython] Slice020_child1  label="Slice020.1"  # WARN: FeaturePython — macro-defined, semantics opaque (R4)
  Base = -> Slice020
  FilterType = 1
  Invert = false
  OverrideMaxVal = 0
  WindowFrom = 80
  WindowTo = 100
  items = 1
FEATURE [Part::Part2DObjectPython] Circle025  # Draft 2D object (typed FeaturePython)
  FirstAngle = 0
  LastAngle = 0
  MakeFace = true
  Placement = pos=(-284.036,162.037,0.266052) rot=(0.57735,0.57735,0.57735;2.0944rad)
  Radius = 2.2
  Support = -> [Extrusion082]
FEATURE [Part::Extrusion] Extrusion084
  Base = -> Circle025
  Dir = (-87.0141,0,0)
  DirMode = 0
  FaceMakerClass = Part::FaceMakerBullseye
  LengthFwd = 0
  LengthRev = 0
  Solid = true
  Symmetric = false
FEATURE [Part::Cut] Cut010012013
  Base = -> Extrusion081
  Tool = -> Extrusion084
FEATURE [Part::Part2DObjectPython] Circle026  # Draft 2D object (typed FeaturePython)
  FirstAngle = 0
  LastAngle = 0
  MakeFace = true
  Placement = pos=(-284.036,162.037,0.266052) rot=(0.57735,0.57735,0.57735;2.0944rad)
  Radius = 2.2
  Support = -> [Extrusion082]
FEATURE [Part::Extrusion] Extrusion085
  Base = -> Circle026
  Dir = (-60.3776,0,0)
  DirMode = 0
  FaceMakerClass = Part::FaceMakerBullseye
  LengthFwd = 0
  LengthRev = 0
  Solid = true
  Symmetric = false
FEATURE [Part::Cut] Cut010012014
  Base = -> Slice020_child1
  Tool = -> Extrusion085
FEATURE [Part::Cut] Cut010012015
  Base = -> Cut010012014
  Tool = -> Extrusion082
FEATURE [Part::MultiFuse] Fusion005002002014004003003002009002010004002003006003008008004003
  Shapes = -> [Cut010012015,Cut010012013]
FEATURE [Part::MultiFuse] Fusion005002002014004003003002009002010004002003006003008008004004
  Shapes = -> [Fusion005002002014004003003002009002010004002003006003008008004002,Fusion005002002014004003003002009002010004002003006003008008004003]
FEATURE [Part::Part2DObjectPython] Rectangle037  # Draft 2D object (typed FeaturePython)
  ChamferSize = 0
  Columns = 1
  FilletRadius = 0
  Height = 0.41625
  Length = 3.63731
  MakeFace = true
  Placement = pos=(-317.078,162.037,15.9498) rot=(0.57735,-0.57735,-0.57735;2.0944rad)
  Rows = 1
FEATURE [Part::Extrusion] Extrusion086
  Base = -> Rectangle037
  Dir = (4.9,0,0)
  DirMode = 0
  FaceMakerClass = Part::FaceMakerBullseye
  LengthFwd = 0
  LengthRev = 0
  Solid = true
  Symmetric = false
FEATURE [Part::MultiFuse] Fusion005002002014004003003002009002010004002003006003008008004005
  Shapes = -> [Extrusion086,Fusion005002002014004003003002009002010004002003006003008008004004]
FEATURE [Part::Part2DObjectPython] Rectangle038  # Draft 2D object (typed FeaturePython)
  ChamferSize = 0
  Columns = 1
  FilletRadius = 0
  Height = 0.41625
  Length = 3.63731
  MakeFace = true
  Placement = pos=(-317.078,162.037,-15.8339) rot=(0.57735,-0.57735,-0.57735;2.0944rad)
  Rows = 1
FEATURE [Part::Extrusion] Extrusion087
  Base = -> Rectangle038
  Dir = (4.9,0,0)
  DirMode = 0
  FaceMakerClass = Part::FaceMakerBullseye
  LengthFwd = 0
  LengthRev = 0
  Solid = true
  Symmetric = false
FEATURE [Part::MultiFuse] Fusion005002002014004003003002009002010004002003006003008008004006
  Shapes = -> [Fusion005002002014004003003002009002010004002003006003008008004005,Extrusion087]
FEATURE [App::DocumentObjectGroup] GrExplode_Slice020  label="Exploded Slice021"
  Group = -> [Fusion005002002014004003003002009002010004002003006003008008004006]
FEATURE [Part::Cone] Cone
  Angle = 360
  AttacherType = Attacher::AttachEngine3D
  Height = 3.5
  Placement = pos=(-252.476,217.863,25.9061) rot=(0,-1,0;1.5708rad)
  Radius1 = 2.2
  Radius2 = 4
FEATURE [Part::Part2DObjectPython] Circle028  # Draft 2D object (typed FeaturePython)
  FirstAngle = 0
  LastAngle = 0
  MakeFace = true
  Placement = pos=(-255.976,217.863,25.9061) rot=(0.57735,0.57735,0.57735;2.0944rad)
  Radius = 16.1
FEATURE [Part::Extrusion] Extrusion088
  Base = -> Circle028
  Dir = (3.5,0,0)
  DirMode = 0
  FaceMakerClass = Part::FaceMakerBullseye
  LengthFwd = 0
  LengthRev = 0
  Solid = true
  Symmetric = false
FEATURE [Part::MultiFuse] Fusion005002002014004003003002009002010004002003006003008008004007
  Shapes = -> [Slice016_child0,Extrusion067,Extrusion068]
FEATURE [Part::Feature] Fusion005002002014004003003002009002010004002003006003008008004007001  label="Fusion005002002014004003003002009002010004002003006003008008004008"
  shape: bbox 61.8 x 32.2 x 20.34 mm, 56 faces (baked)
FEATURE [Part::Feature] Face032
  shape: bbox 2.707e-06 x 32.2 x 20.34 mm, 1 faces, 0 solids (baked)
FEATURE [Part::Extrusion] Extrusion089
  Base = -> Face032
  Dir = (1.5,0,-1.1e-15)
  DirMode = 0
  FaceMakerClass = Part::FaceMakerBullseye
  LengthFwd = 0
  LengthRev = 0
  Solid = true
  Symmetric = false
FEATURE [Part::MultiFuse] Fusion005002002014004003003002009002010004002003006003008008004007002
  Shapes = -> [Extrusion089,Fusion005002002014004003003002009002010004002003006003008008004007001]
FEATURE [Part::Feature] Fusion005002002014004003003002009002010004002003006003008008004007002001  label="Fusion005002002014004003003002009002010004002003006003008008004007003"
  shape: bbox 63.3 x 32.2 x 20.34 mm, 56 faces (baked)
FEATURE [Part::Part2DObjectPython] Rectangle039  # Draft 2D object (typed FeaturePython)
  ChamferSize = 0
  Columns = 1
  FilletRadius = 0
  Height = 32.2
  Length = 3.5
  MakeFace = true
  Placement = pos=(-255.976,201.763,13.2055) rot=(0,0,1;0rad)
  Rows = 1
  Support = -> [Fusion005002002014004003003002009002010004002003006003008008004007002001]
FEATURE [Part::Extrusion] Extrusion090
  Base = -> Rectangle039
  Dir = (1e-15,4e-15,12.7006)
  DirMode = 0
  FaceMakerClass = Part::FaceMakerBullseye
  LengthFwd = 0
  LengthRev = 0
  Solid = true
  Symmetric = false
FEATURE [Part::MultiFuse] Fusion005002002014004003003002009002010004002003006003008008004007002002
  Shapes = -> [Extrusion090,Extrusion088]
FEATURE [Part::Cut] Cut010012016
  Base = -> Fusion005002002014004003003002009002010004002003006003008008004007002002
  Tool = -> Cone
FEATURE [Part::Part2DObjectPython] Rectangle040  # Draft 2D object (typed FeaturePython)
  ChamferSize = 0
  Columns = 1
  FilletRadius = 0
  Height = 24.2
  Length = 13.8
  MakeFace = true
  Placement = pos=(-301.776,205.763,-3.13395) rot=(0,0,1;0rad)
  Rows = 1
FEATURE [Part::Extrusion] Extrusion091
  Base = -> Rectangle040
  Dir = (-5e-16,-1e-16,-2)
  DirMode = 0
  FaceMakerClass = Part::FaceMakerBullseye
  LengthFwd = 0
  LengthRev = 0
  Solid = true
  Symmetric = false
FEATURE [Part::Cut] Cut010012017
  Base = -> Fusion005002002014004003003002009002010004002003006003008008004007002001
  Tool = -> Extrusion091
FEATURE [Part::Part2DObjectPython] Rectangle041  # Draft 2D object (typed FeaturePython)
  ChamferSize = 0
  Columns = 1
  FilletRadius = 0
  Height = 4.67245
  Length = 26.3588
  MakeFace = true
  Placement = pos=(-287.976,227.29,-3.13395) rot=(0,0,1;0rad)
  Rows = 1
FEATURE [Part::Extrusion] Extrusion092
  Base = -> Rectangle041
  Dir = (-5e-16,-1e-16,-2)
  DirMode = 0
  FaceMakerClass = Part::FaceMakerBullseye
  LengthFwd = 0
  LengthRev = 0
  Solid = true
  Symmetric = false
FEATURE [Part::Cut] Cut010012018
  Base = -> Cut010012017
  Tool = -> Extrusion092
FEATURE [Part::Part2DObjectPython] Rectangle042  # Draft 2D object (typed FeaturePython)
  ChamferSize = 0
  Columns = 1
  FilletRadius = 0
  Height = 4.67245
  Length = 26.3588
  MakeFace = true
  Placement = pos=(-287.976,203.763,-3.13395) rot=(0,0,1;0rad)
  Rows = 1
  Support = -> [Cut010012018]
FEATURE [Part::Extrusion] Extrusion093
  Base = -> Rectangle042
  Dir = (-5e-16,-1e-16,-2)
  DirMode = 0
  FaceMakerClass = Part::FaceMakerBullseye
  LengthFwd = 0
  LengthRev = 0
  Solid = true
  Symmetric = false
FEATURE [Part::Cut] Cut010012019
  Base = -> Cut010012018
  Tool = -> Extrusion093
FEATURE [Part::Part2DObjectPython] Rectangle043  # Draft 2D object (typed FeaturePython)
  ChamferSize = 0
  Columns = 1
  FilletRadius = 0
  Height = 18.8551
  Length = 9.59764
  MakeFace = true
  Placement = pos=(-265.574,208.435,-3.13395) rot=(0,0,1;0rad)
  Rows = 1
FEATURE [Part::Extrusion] Extrusion094
  Base = -> Rectangle043
  Dir = (-5e-16,-1e-16,-2)
  DirMode = 0
  FaceMakerClass = Part::FaceMakerBullseye
  LengthFwd = 0
  LengthRev = 0
  Solid = true
  Symmetric = false
FEATURE [Part::Cut] Cut010012020
  Base = -> Cut010012019
  Tool = -> Extrusion094
FEATURE [Part::Part2DObjectPython] Wire007  # Draft 2D object (typed FeaturePython)
  ChamferSize = 0
  Closed = true
  End = (-287.976,205.763,-3.13395)
  FilletRadius = 0
  Length = 15.0822
  MakeFace = true
  Placement = pos=(-287.976,203.763,-3.13395) rot=(0,0,1;0rad)
  Points = (3) [(0,0,0),(-6.38822,2,-3.55271e-14),(0,2,-3.37508e-14)]
  Start = (-287.976,203.763,-3.13395)
  Subdivisions = 0
FEATURE [Part::Extrusion] Extrusion095
  Base = -> Wire007
  Dir = (-2e-16,-3.48e-14,-2)
  DirMode = 0
  FaceMakerClass = Part::FaceMakerBullseye
  LengthFwd = 0
  LengthRev = 0
  Solid = true
  Symmetric = false
FEATURE [Part::Cut] Cut010012021
  Base = -> Cut010012020
  Tool = -> Extrusion095
FEATURE [Part::Part2DObjectPython] Wire008  # Draft 2D object (typed FeaturePython)
  ChamferSize = 0
  Closed = true
  End = (-287.976,229.963,-3.13395)
  FilletRadius = 0
  Length = 15.0822
  MakeFace = true
  Placement = pos=(-287.976,231.963,-3.13395) rot=(0,0,1;0rad)
  Points = (3) [(0,0,0),(-6.38822,-2,-3.41949e-14),(0,-2,-3.41949e-14)]
  Start = (-287.976,231.963,-3.13395)
  Subdivisions = 0
  Support = -> [Cut010012021]
FEATURE [Part::Extrusion] Extrusion096
  Base = -> Wire008
  Dir = (-5e-16,3.41e-14,-2)
  DirMode = 0
  FaceMakerClass = Part::FaceMakerBullseye
  LengthFwd = 0
  LengthRev = 0
  Solid = true
  Symmetric = false
FEATURE [Part::Cut] Cut010012022
  Base = -> Cut010012021
  Tool = -> Extrusion096
FEATURE [Part::MultiFuse] Fusion005002002014004003003002009002010004002003006003008008004007002003
  Shapes = -> [Cut010012022,Cut010012010]
FEATURE [Part::MultiFuse] Fusion005002002014004003003002009002010004002003006003008008004007002004
  Shapes = -> [Fusion005002002014004003003002009002010004002003006003008008004007002003,Cut010012016]
FEATURE [Part::Feature] Fusion005002002014004003003002009002010004002003006003008008004007002004001  label="Fusion005002002014004003003002009002010004002003006003008008004007002005"
  Placement = pos=(18.3807,-36.325,7.1e-15) rot=(0,0,1;0rad)
  shape: bbox 63.3 x 32.2 x 49.14 mm, 71 faces (baked)
FEATURE [Part::Feature] Fusion005002002014004003003002009002010004002003006003008008004006001  label="Fusion005002002014004003003002009002010004002003006003008008004007002006"
  Placement = pos=(2.35263,-3.74708,8.7) rot=(0,0,1;0rad)
  shape: bbox 29.99 x 49.14 x 32.2 mm, 47 faces (baked)
FEATURE [Part::Feature] Fusion005002002014004003003002009002010004002003006003008008004007002004008002001  label="Fusion005002002014004003003002009002010004002003006003008008004007002004008003"
  Placement = pos=(10.6042,128.634,6.8e-14) rot=(0,0,1;0rad)
  shape: bbox 33.39 x 29.4 x 32.2 mm, 46 faces (baked)
FEATURE [Part::MultiFuse] Fusion005002002014004003003002009002010004002003006003008008004007002004008002003
  Placement = pos=(23.3292,204.079,-1) rot=(0,0,1;0rad)
  Shapes = -> [Slice014_child0,Slice013_child0]
FEATURE [Part::MultiFuse] Fusion005002002014004003003002009002010004002003006003008008004007002004008002004
  Placement = pos=(22.9562,204.066,-1) rot=(0,0,1;0rad)
  Shapes = -> [Slice011_child1,Slice012_child0]
FEATURE [Part::Feature] Fusion005002002014004003003002009002010004002003006003008008004007002004008002005003003  label="Fusion005002002014004003003002009002010004002003006003008008004007002004008002005006"
  shape: bbox 62.3 x 53.48 x 32.2 mm, 75 faces (baked)
